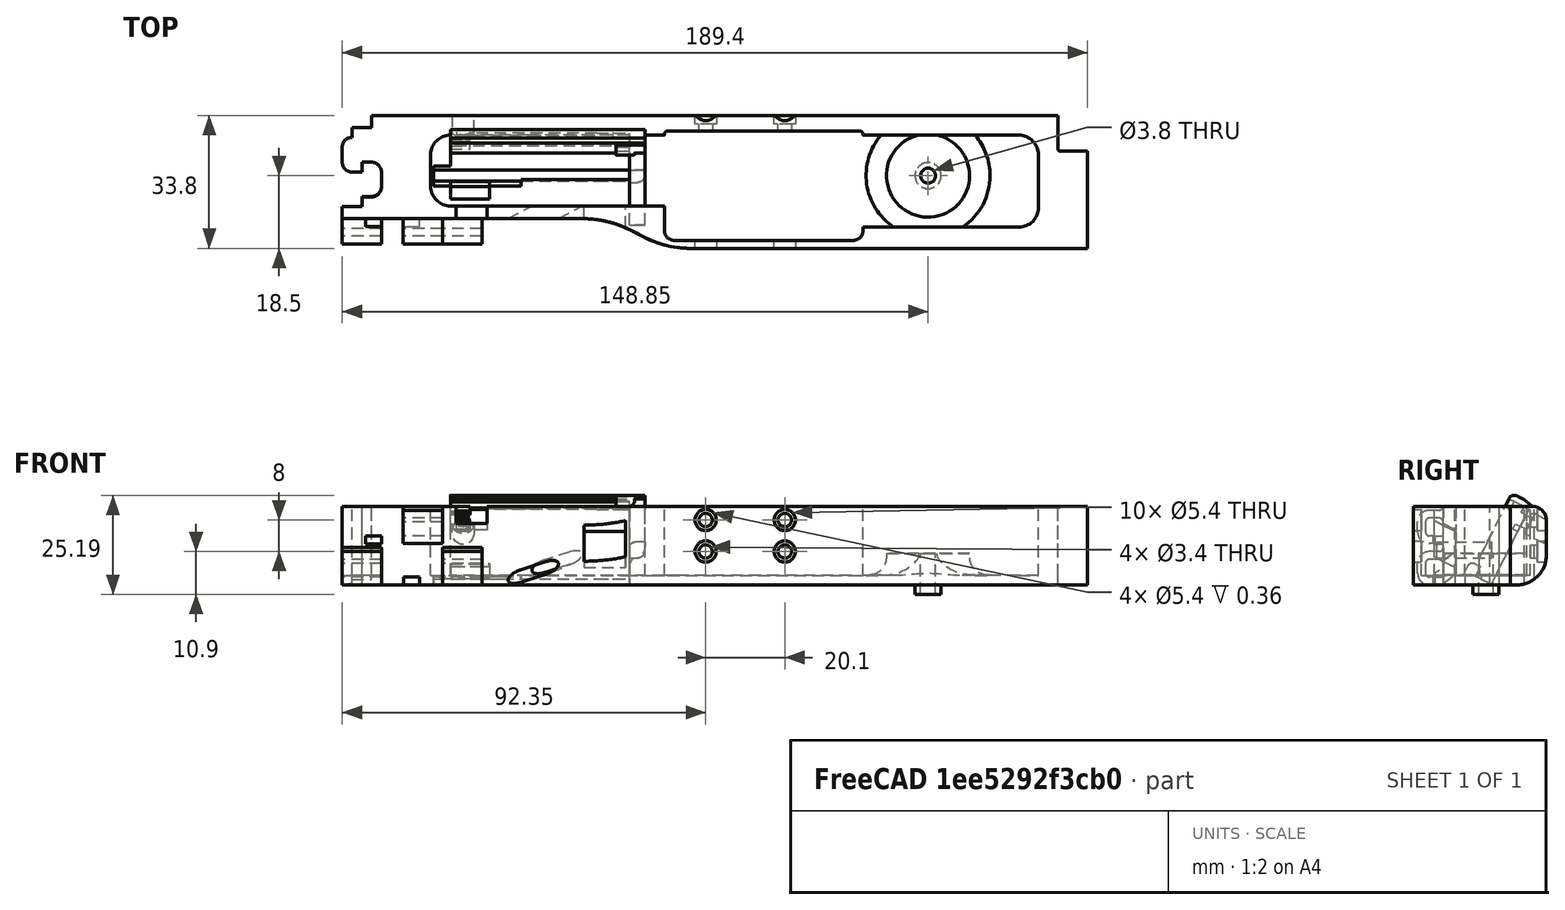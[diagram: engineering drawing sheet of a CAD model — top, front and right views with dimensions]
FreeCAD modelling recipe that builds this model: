
FCSTD DOCUMENT  (FreeCAD 0.19R0.19.2)
Label: rightSideV1_1
License: All rights reserved
LicenseURL: http://en.wikipedia.org/wiki/All_rights_reserved
objects: Sketcher::SketchObject×45, Part::Extrusion×35, Part::MultiFuse×22, Part::Box×19, Part::Cut×16, Part::Fillet×14, App::MeasureDistance×10, Part::Cylinder×4, Part::Revolution×1, Mesh::Feature×1
note: 156 computed .brp shape members not serialized (recipe doc carries the construction recipe); baked Part::Feature solids carry a one-line shape summary decoded from their .brp

FEATURE [Sketcher::SketchObject] Sketch
  FullyConstrained = true
  sketch-geometry (36):
    g0: LineSegment StartX=0 StartY=0 StartZ=0 EndX=154.4 EndY=0 EndZ=0
    g1: LineSegment StartX=154.4 StartY=0 StartZ=0 EndX=154.4 EndY=-7.6 EndZ=0
    g2: LineSegment StartX=32.5209 StartY=-26.2 StartZ=0 EndX=-7.5 EndY=-26.2 EndZ=0
    g3-g7: Circle x5 (B-spline internal-alignment scaffolding for g8; pole/knot coordinates omitted)
    g8: BSplineCurve PolesCount=5 KnotsCount=3 Degree=3 IsPeriodic=0
    g9: GeomPoint X=61.85 Y=-33.8 Z=0
    g10: GeomPoint X=47.185 Y=-29.9 Z=0
    g11: GeomPoint X=32.5209 Y=-26.2 Z=0
    g12: Circle CenterX=121.35 CenterY=-14.3 CenterZ=0 NormalX=0 NormalY=0 NormalZ=1 AngleXU=0 Radius=3.25
    g13: LineSegment StartX=-7.5 StartY=-26.2 StartZ=0 EndX=-27.5 EndY=-26.2 EndZ=0
    g14: LineSegment StartX=-20 StartY=0 StartZ=0 EndX=0 EndY=0 EndZ=0
    g15: LineSegment StartX=-25 StartY=-3.1 StartZ=0 EndX=-20 EndY=-3.1 EndZ=0
    g16: LineSegment StartX=-25 StartY=-3.1 StartZ=0 EndX=-25 EndY=-5.6 EndZ=0
    g17: LineSegment StartX=-27.5 StartY=-8.1 StartZ=0 EndX=-27.5 EndY=-11.85 EndZ=0
    g18: ArcOfCircle CenterX=-25 CenterY=-8.1 CenterZ=0 NormalX=0 NormalY=0 NormalZ=1 AngleXU=0 Radius=2.5 StartAngle=1.5708 EndAngle=3.14159
    g19: LineSegment StartX=-25 StartY=-14.35 StartZ=0 EndX=-22.5 EndY=-14.35 EndZ=0
    g20: ArcOfCircle CenterX=-25 CenterY=-11.85 CenterZ=0 NormalX=0 NormalY=0 NormalZ=1 AngleXU=0 Radius=2.5 StartAngle=3.14159 EndAngle=4.71239
    g21: LineSegment StartX=-22.5 StartY=-14.35 StartZ=0 EndX=-22.5 EndY=-11.85 EndZ=0
    g22: LineSegment StartX=-22.5 StartY=-11.85 StartZ=0 EndX=-20 EndY=-11.85 EndZ=0
    g23: ArcOfCircle CenterX=-20 CenterY=-14.35 CenterZ=0 NormalX=0 NormalY=0 NormalZ=1 AngleXU=0 Radius=2.5 StartAngle=8e-16 EndAngle=1.5708
    g24: LineSegment StartX=-17.5 StartY=-14.35 StartZ=0 EndX=-17.5 EndY=-18.1 EndZ=0
    g25: ArcOfCircle CenterX=-20 CenterY=-18.1 CenterZ=0 NormalX=0 NormalY=0 NormalZ=1 AngleXU=0 Radius=2.5 StartAngle=4.71239 EndAngle=6.28319
    g26: LineSegment StartX=-22.5 StartY=-20.6 StartZ=0 EndX=-20 EndY=-20.6 EndZ=0
    g27: LineSegment StartX=-22.5 StartY=-20.6 StartZ=0 EndX=-22.5 EndY=-23.1 EndZ=0
    g28: LineSegment StartX=-27.5 StartY=-23.1 StartZ=0 EndX=-22.5 EndY=-23.1 EndZ=0
    g29: LineSegment StartX=-20 StartY=-3.1 StartZ=0 EndX=-20 EndY=0 EndZ=0
    g30: LineSegment StartX=-27.5 StartY=-23.1 StartZ=0 EndX=-27.5 EndY=-26.2 EndZ=0
    g31: LineSegment StartX=154.4 StartY=-7.6 StartZ=0 EndX=154.4 EndY=-8.6 EndZ=0
    g32: ArcOfCircle CenterX=154.9 CenterY=-8.6 CenterZ=0 NormalX=0 NormalY=0 NormalZ=1 AngleXU=0 Radius=0.5 StartAngle=3.14159 EndAngle=4.71239
    g33: LineSegment StartX=154.9 StartY=-9.1 StartZ=0 EndX=161.9 EndY=-9.1 EndZ=0
    g34: LineSegment StartX=161.9 StartY=-9.1 StartZ=0 EndX=161.9 EndY=-33.8 EndZ=0
    g35: LineSegment StartX=161.9 StartY=-33.8 StartZ=0 EndX=61.85 EndY=-33.8 EndZ=0
  constraints (72):
    c: PointOnObject(g0,g-2)
    c: Horizontal(g0)
    c: Distance(g0) = 154.4
    c: DistanceY(g-1,g0) = 0
    c: Vertical(g1)
    c: Distance(g1) = 7.6
    c: Coincident(g1,g0)
    c: Horizontal(g2)
    c: Block(g2)
    c: Weight(g3) = 1
    c: Coincident(g8,g2)
    c: InternalAlignment(g3-g7 -> g8) x5
    c: InternalAlignment(g9,g8)
    c: InternalAlignment(g10,g8)
    c: InternalAlignment(g11,g8)
    c: Block(g12)
    c: Coincident(g13,g2)
    c: Horizontal(g13)
    c: Distance(g13) = 20
    c: Horizontal(g14)
    c: Distance(g14) = 20
    c: Coincident(g14,g0)
    c: Horizontal(g15)
    c: Vertical(g16)
    c: Coincident(g16,g15)
    c: Vertical(g17)
    c: Coincident(g18,g16)
    c: Block(g18)
    c: Coincident(g17,g18)
    c: Horizontal(g19)
    c: Coincident(g20,g17)
    c: Block(g20)
    c: Block(g19)
    c: Vertical(g21)
    c: Coincident(g21,g19)
    c: Horizontal(g22)
    c: Coincident(g22,g21)
    c: Coincident(g23,g22)
    c: Vertical(g24)
    c: Block(g23)
    c: Coincident(g24,g23)
    c: Coincident(g25,g24)
    c: Block(g25)
    c: Horizontal(g26)
    c: Coincident(g26,g25)
    c: Vertical(g27)
    c: Coincident(g27,g26)
    c: Horizontal(g28)
    c: Coincident(g28,g27)
    c: Block(g15)
    c: Block(g28)
    c: Coincident(g29,g15)
    c: Coincident(g29,g14)
    c: Vertical(g29)
    c: Coincident(g30,g28)
    c: Coincident(g30,g13)
    c: Vertical(g30)
    c: Vertical(g31)
    c: Distance(g31) = 1
    c: Coincident(g31,g1)
    c: Coincident(g32,g31)
    c: Block(g32)
    c: Coincident(g33,g32)
    c: Horizontal(g33)
    c: Coincident(g34,g33)
    c: Vertical(g34)
    c: Block(g34)
    c: Coincident(g35,g34)
    c: Horizontal(g35)
    c: Block(g35)
    c: Coincident(g8,g35)
    c: Block(g8)
FEATURE [Part::Extrusion] Extrude  label="mainBodyBaseExtrude"
  Base = -> Sketch
  Dir = (0,0,1)
  DirMode = 2
  FaceMakerClass = Part::FaceMakerBullseye
  LengthFwd = 2.4
  LengthRev = 0
  Solid = true
  Symmetric = false
FEATURE [Sketcher::SketchObject] Sketch001
  FullyConstrained = true
  sketch-geometry (75):
    g0: ArcOfCircle CenterX=144.4 CenterY=-10 CenterZ=0 NormalX=0 NormalY=0 NormalZ=1 AngleXU=0 Radius=5 StartAngle=4.345e-13 EndAngle=1.5708
    g1: LineSegment StartX=32.5209 StartY=-26.2 StartZ=0 EndX=-7.49911 EndY=-26.2 EndZ=0
    g2: LineSegment StartX=0 StartY=0 StartZ=0 EndX=154.4 EndY=0 EndZ=0
    g3-g7: Circle x5 (B-spline internal-alignment scaffolding for g8; pole/knot coordinates omitted)
    g8: BSplineCurve PolesCount=5 KnotsCount=3 Degree=3 IsPeriodic=0
    g9: GeomPoint X=61.85 Y=-33.8 Z=0
    g10: GeomPoint X=47.1857 Y=-29.9 Z=0
    g11: GeomPoint X=32.5209 Y=-26.2 Z=0
    g12: LineSegment StartX=154.4 StartY=0 StartZ=0 EndX=154.4 EndY=-7.6 EndZ=0
    g13: LineSegment StartX=20 StartY=-5 StartZ=0 EndX=54.35 EndY=-5 EndZ=0
    g14: LineSegment StartX=104.85 StartY=-5 StartZ=0 EndX=144.4 EndY=-5 EndZ=0
    g15: LineSegment StartX=54.35 StartY=-23 StartZ=0 EndX=20 EndY=-23 EndZ=0
    g16: LineSegment StartX=-27.4991 StartY=-26.2 StartZ=0 EndX=-7.49911 EndY=-26.2 EndZ=0
    g17: LineSegment StartX=-20 StartY=0 StartZ=0 EndX=0 EndY=0 EndZ=0
    g18: LineSegment StartX=-27.4991 StartY=-23.2 StartZ=0 EndX=-22.5 EndY=-23.2 EndZ=0
    g19: LineSegment StartX=-22.5 StartY=-20.7 StartZ=0 EndX=-22.5 EndY=-23.2 EndZ=0
    g20: LineSegment StartX=-22.5 StartY=-20.7 StartZ=0 EndX=-20 EndY=-20.7 EndZ=0
    g21: ArcOfCircle CenterX=-20 CenterY=-18.2 CenterZ=0 NormalX=0 NormalY=0 NormalZ=1 AngleXU=0 Radius=2.5 StartAngle=4.71239 EndAngle=6.28319
    g22: LineSegment StartX=-17.5 StartY=-14.4 StartZ=0 EndX=-17.5 EndY=-18.2 EndZ=0
    g23: ArcOfCircle CenterX=-20 CenterY=-14.4 CenterZ=0 NormalX=0 NormalY=0 NormalZ=1 AngleXU=0 Radius=2.5 StartAngle=9e-16 EndAngle=1.5708
    g24: LineSegment StartX=-22.5 StartY=-11.9 StartZ=0 EndX=-20 EndY=-11.9 EndZ=0
    g25: LineSegment StartX=-22.5 StartY=-14.4 StartZ=0 EndX=-22.5 EndY=-11.9 EndZ=0
    g26: LineSegment StartX=-25 StartY=-14.4 StartZ=0 EndX=-22.5 EndY=-14.4 EndZ=0
    g27: ArcOfCircle CenterX=-25 CenterY=-11.9 CenterZ=0 NormalX=0 NormalY=0 NormalZ=1 AngleXU=0 Radius=2.5 StartAngle=3.14159 EndAngle=4.71239
    g28: LineSegment StartX=-27.5 StartY=-8.1 StartZ=0 EndX=-27.5 EndY=-11.9 EndZ=0
    g29: ArcOfCircle CenterX=-25 CenterY=-8.1 CenterZ=0 NormalX=0 NormalY=0 NormalZ=1 AngleXU=0 Radius=2.5 StartAngle=1.5708 EndAngle=3.14159
    g30: LineSegment StartX=-25 StartY=-3.1 StartZ=0 EndX=-25 EndY=-5.6 EndZ=0
    g31: LineSegment StartX=-20 StartY=-3.1 StartZ=0 EndX=-25 EndY=-3.1 EndZ=0
    g32: LineSegment StartX=-20 StartY=0 StartZ=0 EndX=-20 EndY=-3.1 EndZ=0
    g33: LineSegment StartX=-27.4991 StartY=-26.2 StartZ=0 EndX=-27.4991 EndY=-23.2 EndZ=0
    g34: LineSegment StartX=4.09e-14 StartY=-5 StartZ=0 EndX=20 EndY=-5 EndZ=0
    g35: ArcOfCircle CenterX=7.1e-15 CenterY=-18 CenterZ=0 NormalX=0 NormalY=0 NormalZ=1 AngleXU=0 Radius=5 StartAngle=3.14159 EndAngle=4.71239
    g36: ArcOfCircle CenterX=4.26e-14 CenterY=-10 CenterZ=0 NormalX=0 NormalY=0 NormalZ=1 AngleXU=0 Radius=5 StartAngle=1.5708 EndAngle=3.14159
    g37: LineSegment StartX=-5 StartY=-18 StartZ=0 EndX=-5 EndY=-10 EndZ=0
    g38: LineSegment StartX=6.2e-15 StartY=-23 StartZ=0 EndX=20 EndY=-23 EndZ=0
    g39: LineSegment StartX=154.4 StartY=-7.6 StartZ=0 EndX=154.4 EndY=-8.6 EndZ=0
    g40: LineSegment StartX=154.9 StartY=-9.1 StartZ=0 EndX=161.9 EndY=-9.1 EndZ=0
    g41: ArcOfCircle CenterX=154.9 CenterY=-8.6 CenterZ=0 NormalX=0 NormalY=0 NormalZ=1 AngleXU=0 Radius=0.5 StartAngle=3.14159 EndAngle=4.71299
    g42: LineSegment StartX=104.85 StartY=-28.3916 StartZ=0 EndX=144.408 EndY=-28.3916 EndZ=0
    g43: LineSegment StartX=149.4 StartY=-10 StartZ=0 EndX=149.4 EndY=-23.4 EndZ=0
    g44: ArcOfCircle CenterX=144.408 CenterY=-23.4 CenterZ=0 NormalX=0 NormalY=0 NormalZ=1 AngleXU=0 Radius=4.99164 StartAngle=4.71239 EndAngle=6.28319
    g45: LineSegment StartX=104.85 StartY=-28.3916 StartZ=0 EndX=104.85 EndY=-28.7833 EndZ=0
    g46: LineSegment StartX=54.35 StartY=-28.7916 StartZ=0 EndX=54.35 EndY=-23 EndZ=0
    g47: LineSegment StartX=161.9 StartY=-33.8 StartZ=0 EndX=161.9 EndY=-9.1 EndZ=0
    g48: LineSegment StartX=61.85 StartY=-33.8 StartZ=0 EndX=161.9 EndY=-33.8 EndZ=0
    g49: Circle CenterX=54.35 CenterY=-28.7916 CenterZ=0 NormalX=0 NormalY=0 NormalZ=1 AngleXU=0 Radius=1
    g50: Circle CenterX=54.35 CenterY=-31.7916 CenterZ=0 NormalX=0 NormalY=0 NormalZ=1 AngleXU=0 Radius=1
    g51: Circle CenterX=57.35 CenterY=-31.7916 CenterZ=0 NormalX=0 NormalY=0 NormalZ=1 AngleXU=0 Radius=1
    g52: BSplineCurve PolesCount=3 KnotsCount=2 Degree=2 IsPeriodic=0
    g53: GeomPoint X=54.35 Y=-28.7916 Z=0
    g54: GeomPoint X=57.35 Y=-31.7916 Z=0
    g55: Circle CenterX=104.85 CenterY=-28.7833 CenterZ=0 NormalX=0 NormalY=0 NormalZ=1 AngleXU=0 Radius=1
    g56: Circle CenterX=104.85 CenterY=-31.7916 CenterZ=0 NormalX=0 NormalY=0 NormalZ=1 AngleXU=0 Radius=1
    g57: Circle CenterX=101.85 CenterY=-31.7916 CenterZ=0 NormalX=0 NormalY=0 NormalZ=1 AngleXU=0 Radius=1
    g58: BSplineCurve PolesCount=3 KnotsCount=2 Degree=2 IsPeriodic=0
    g59: GeomPoint X=104.85 Y=-28.7833 Z=0
    g60: GeomPoint X=101.85 Y=-31.7916 Z=0
    g61: LineSegment StartX=57.35 StartY=-31.7916 StartZ=0 EndX=101.85 EndY=-31.7916 EndZ=0
    g62: Circle CenterX=54.35 CenterY=-5 CenterZ=0 NormalX=0 NormalY=0 NormalZ=1 AngleXU=0 Radius=1
    g63: Circle CenterX=54.35 CenterY=-4 CenterZ=0 NormalX=0 NormalY=0 NormalZ=1 AngleXU=0 Radius=1
    g64: Circle CenterX=55.15 CenterY=-4 CenterZ=0 NormalX=0 NormalY=0 NormalZ=1 AngleXU=0 Radius=1
    g65: BSplineCurve PolesCount=3 KnotsCount=2 Degree=2 IsPeriodic=0
    g66: GeomPoint X=54.35 Y=-5 Z=0
    g67: GeomPoint X=55.15 Y=-4 Z=0
    g68: Circle CenterX=104.85 CenterY=-5 CenterZ=0 NormalX=0 NormalY=0 NormalZ=1 AngleXU=0 Radius=1
    g69: Circle CenterX=104.85 CenterY=-4 CenterZ=0 NormalX=0 NormalY=0 NormalZ=1 AngleXU=0 Radius=1
    g70: Circle CenterX=104.05 CenterY=-4 CenterZ=0 NormalX=0 NormalY=0 NormalZ=1 AngleXU=0 Radius=1
    g71: BSplineCurve PolesCount=3 KnotsCount=2 Degree=2 IsPeriodic=0
    g72: GeomPoint X=104.85 Y=-5 Z=0
    g73: GeomPoint X=104.05 Y=-4 Z=0
    g74: LineSegment StartX=104.05 StartY=-4 StartZ=0 EndX=55.15 EndY=-4 EndZ=0
  constraints (156):
    c: PointOnObject(g2,g-2)
    c: DistanceY(g-1,g2) = 0
    c: Block(g0)
    c: Horizontal(g1)
    c: Distance(g1) = 40.02
    c: Horizontal(g2)
    c: Block(g2)
    c: Weight(g3) = 1
    c: Equal(g3, g4-g7) x4
    c: Coincident(g8,g1)
    c: InternalAlignment(g3-g7 -> g8) x5
    c: InternalAlignment(g9,g8)
    c: InternalAlignment(g10,g8)
    c: InternalAlignment(g11,g8)
    c: Vertical(g12)
    c: Coincident(g12,g2)
    c: Distance(g12) = 7.6
    c: Block(g12)
    c: Horizontal(g13)
    c: Coincident(g14,g0)
    c: Horizontal(g14)
    c: Horizontal(g15)
    c: Horizontal(g16)
    c: Distance(g16) = 20
    c: Coincident(g1,g16)
    c: Horizontal(g17)
    c: Distance(g17) = 20
    c: Coincident(g17,g2)
    c: Horizontal(g31)
    c: Vertical(g30)
    c: Coincident(g29,g30)
    c: Vertical(g28)
    c: Block(g29)
    c: Coincident(g27,g28)
    c: Block(g27)
    c: Horizontal(g26)
    c: Coincident(g26,g27)
    c: Vertical(g25)
    c: Coincident(g25,g26)
    c: Horizontal(g24)
    c: Coincident(g23,g24)
    c: Block(g23)
    c: Vertical(g22)
    c: Coincident(g21,g22)
    c: Block(g21)
    c: Horizontal(g20)
    c: Coincident(g20,g21)
    c: Vertical(g19)
    c: Coincident(g19,g20)
    c: Horizontal(g18)
    c: Coincident(g18,g19)
    c: Coincident(g32,g17)
    c: Coincident(g32,g31)
    c: Vertical(g32)
    c: Coincident(g33,g16)
    c: Coincident(g33,g18)
    c: Vertical(g33)
    c: Block(g33)
    c: Block(g18)
    c: Block(g22)
    c: Block(g26)
    c: Block(g25)
    c: Block(g24)
    c: Block(g28)
    c: Block(g31)
    c: Block(g30)
    c: Horizontal(g34)
    c: Distance(g34) = 20
    c: Block(g35)
    c: Block(g36)
    c: Coincident(g37,g35)
    c: Coincident(g37,g36)
    c: Vertical(g37)
    c: Coincident(g38,g35)
    c: Coincident(g38,g15)
    c: Horizontal(g38)
    c: Block(g38)
    c: Block(g34)
    c: Block(g13)
    c: Vertical(g39)
    c: Distance(g39) = 1
    c: Coincident(g39,g12)
    c: Horizontal(g40)
    c: Coincident(g41,g39)
    c: Coincident(g41,g40)
    c: Block(g39)
    c: Block(g41)
    c: Horizontal(g42)
    c: Vertical(g43)
    c: Distance(g43) = 13.4
    c: Coincident(g43,g0)
    c: Block(g42)
    c: Block(g43)
    c: Coincident(g44,g43)
    c: Coincident(g44,g42)
    c: Block(g44)
    c: Distance(g15) = 34.35
    c: Coincident(g45,g42)
    c: Vertical(g45)
    c: Coincident(g46,g15)
    c: Vertical(g46)
    c: Coincident(g47,g40)
    c: Vertical(g47)
    c: Block(g47)
    c: Coincident(g48,g47)
    c: Horizontal(g48)
    c: Block(g48)
    c: Coincident(g8,g48)
    c: Block(g8)
    c: Coincident(g52,g46)
    c: Weight(g49) = 1
    c: Equal(g49,g50)
    c: Equal(g49,g51)
    c: InternalAlignment(g49,g52)
    c: InternalAlignment(g50,g52)
    c: InternalAlignment(g51,g52)
    c: InternalAlignment(g53,g52)
    c: InternalAlignment(g54,g52)
    c: Coincident(g58,g45)
    c: Weight(g55) = 1
    c: Equal(g55,g56)
    c: Equal(g55,g57)
    c: InternalAlignment(g55,g58)
    c: InternalAlignment(g56,g58)
    c: InternalAlignment(g57,g58)
    c: InternalAlignment(g59,g58)
    c: InternalAlignment(g60,g58)
    c: Block(g58)
    c: Block(g52)
    c: Coincident(g61,g52)
    c: Coincident(g61,g58)
    c: Horizontal(g61)
    c: Block(g14)
    c: Coincident(g65,g13)
    c: Weight(g62) = 1
    c: Equal(g62,g63)
    c: Equal(g62,g64)
    c: InternalAlignment(g62,g65)
    c: InternalAlignment(g63,g65)
    c: InternalAlignment(g64,g65)
    c: InternalAlignment(g66,g65)
    c: InternalAlignment(g67,g65)
    c: Block(g65)
    c: Coincident(g71,g14)
    c: Weight(g68) = 1
    c: Equal(g68,g69)
    c: Equal(g68,g70)
    c: InternalAlignment(g68,g71)
    c: InternalAlignment(g69,g71)
    c: InternalAlignment(g70,g71)
    c: InternalAlignment(g72,g71)
    c: InternalAlignment(g73,g71)
    c: Block(g71)
    c: Coincident(g74,g71)
    c: Coincident(g74,g65)
    c: Horizontal(g74)
FEATURE [Sketcher::SketchObject] Sketch005
  FullyConstrained = true
  Placement = pos=(0,0,0) rot=(1,0,0;1.5708rad)
  sketch-geometry (4):
    g0: Circle CenterX=84.95 CenterY=16.5 CenterZ=0 NormalX=0 NormalY=0 NormalZ=1 AngleXU=0 Radius=1.7
    g1: Circle CenterX=84.95 CenterY=8.5 CenterZ=0 NormalX=0 NormalY=0 NormalZ=1 AngleXU=0 Radius=1.7
    g2: Circle CenterX=64.85 CenterY=8.5 CenterZ=0 NormalX=0 NormalY=0 NormalZ=1 AngleXU=0 Radius=1.7
    g3: Circle CenterX=64.85 CenterY=16.5 CenterZ=0 NormalX=0 NormalY=0 NormalZ=1 AngleXU=0 Radius=1.7
  constraints (4):
    c: Block(g0)
    c: Block(g1)
    c: Block(g2)
    c: Block(g3)
FEATURE [Part::Extrusion] Extrude004  label="removeFromMainBodyToCreateScrewHolesForSolenoidExtrude004"
  Base = -> Sketch005
  Dir = (0,-1,1.1e-15)
  DirMode = 2
  FaceMakerClass = Part::FaceMakerBullseye
  LengthFwd = 10
  LengthRev = 0
  Solid = true
  Symmetric = false
FEATURE [Sketcher::SketchObject] Sketch004
  FullyConstrained = true
  Placement = pos=(0,0,0) rot=(1,0,0;1.5708rad)
  sketch-geometry (12):
    g0: LineSegment StartX=15.75 StartY=2.5 StartZ=0 EndX=15.75 EndY=0 EndZ=0
    g1: Circle CenterX=15.75 CenterY=2.5 CenterZ=0 NormalX=0 NormalY=0 NormalZ=1 AngleXU=0 Radius=1
    g2: Circle CenterX=10.55 CenterY=2.5 CenterZ=0 NormalX=0 NormalY=0 NormalZ=1 AngleXU=0 Radius=1
    g3: Circle CenterX=10.55 CenterY=8 CenterZ=0 NormalX=0 NormalY=0 NormalZ=1 AngleXU=0 Radius=1
    g4: BSplineCurve PolesCount=3 KnotsCount=2 Degree=2 IsPeriodic=0
    g5: GeomPoint X=15.75 Y=2.5 Z=0
    g6: GeomPoint X=10.55 Y=8 Z=0
    g7: LineSegment StartX=1.9 StartY=8 StartZ=0 EndX=10.55 EndY=8 EndZ=0
    g8: LineSegment StartX=1.9 StartY=-2.4 StartZ=0 EndX=1.9 EndY=8 EndZ=0
    g9: LineSegment StartX=3.30092 StartY=-2.4 StartZ=0 EndX=3.30092 EndY=0 EndZ=0
    g10: LineSegment StartX=15.75 StartY=0 StartZ=0 EndX=3.30092 EndY=0 EndZ=0
    g11: LineSegment StartX=3.30092 StartY=-2.4 StartZ=0 EndX=1.9 EndY=-2.4 EndZ=0
  constraints (26):
    c: Vertical(g0)
    c: Distance(g0) = 2.5
    c: Coincident(g4,g0)
    c: Weight(g1) = 1
    c: Equal(g1,g2)
    c: Equal(g1,g3)
    c: InternalAlignment(g1,g4)
    c: InternalAlignment(g2,g4)
    c: InternalAlignment(g3,g4)
    c: InternalAlignment(g5,g4)
    c: InternalAlignment(g6,g4)
    c: Block(g4)
    c: Coincident(g7,g4)
    c: Horizontal(g7)
    c: Vertical(g8)
    c: Coincident(g8,g7)
    c: Block(g8)
    c: Vertical(g9)
    c: Coincident(g10,g0)
    c: PointOnObject(g10,g-1)
    c: Horizontal(g10)
    c: Coincident(g10,g9)
    c: Block(g9)
    c: Coincident(g11,g9)
    c: Coincident(g11,g8)
    c: Horizontal(g11)
FEATURE [Sketcher::SketchObject] Sketch007
  FullyConstrained = true
  Placement = pos=(0,-14.3,2.37) rot=(-1,0,0;2.03453rad)
  sketch-geometry (6):
    g0: LineSegment StartX=0 StartY=0 StartZ=0 EndX=45.5 EndY=0 EndZ=0
    g1: LineSegment StartX=0 StartY=0 StartZ=0 EndX=0 EndY=-21.2 EndZ=0
    g2: LineSegment StartX=45.5 StartY=0 StartZ=0 EndX=49.5 EndY=0 EndZ=0
    g3: LineSegment StartX=49.5 StartY=0 StartZ=0 EndX=49.5 EndY=-21.2 EndZ=0
    g4: LineSegment StartX=49.5 StartY=-21.2 StartZ=0 EndX=0 EndY=-21.2 EndZ=0
    g5: Circle CenterX=3.25 CenterY=-18.05 CenterZ=0 NormalX=0 NormalY=0 NormalZ=1 AngleXU=0 Radius=1.6
  constraints (15):
    c: Coincident(g0,g-1)
    c: Horizontal(g0)
    c: Distance(g0) = 45.5
    c: Coincident(g1,g0)
    c: Vertical(g1)
    c: Horizontal(g2)
    c: Distance(g2) = 4
    c: Coincident(g2,g0)
    c: Coincident(g3,g2)
    c: Vertical(g3)
    c: Block(g3)
    c: Coincident(g4,g3)
    c: Horizontal(g4)
    c: Coincident(g4,g1)
    c: Block(g5)
FEATURE [Part::Extrusion] Extrude005  label="solenoidDriverHolderExtrude005"
  Base = -> Sketch007
  Dir = (0,0.894389,-0.447291)
  DirMode = 2
  FaceMakerClass = Part::FaceMakerBullseye
  LengthFwd = 10
  LengthRev = 0
  Placement = pos=(0,0,-2) rot=(0,0,1;0rad)
  Solid = true
  Symmetric = false
FEATURE [Sketcher::SketchObject] Sketch008
  FullyConstrained = false
  Placement = pos=(0,-4.3,-2.6) rot=(-1,0,0;2.03453rad)
  sketch-geometry (1):
    g0: Circle CenterX=42.25 CenterY=-3.15 CenterZ=0 NormalX=0 NormalY=0 NormalZ=1 AngleXU=0 Radius=4.5
FEATURE [Sketcher::SketchObject] Sketch009
  FullyConstrained = true
  Placement = pos=(0,-4.3,-2.6) rot=(-1,0,0;2.03453rad)
  sketch-geometry (1):
    g0: Circle CenterX=3.25 CenterY=-18.0217 CenterZ=0 NormalX=0 NormalY=0 NormalZ=1 AngleXU=0 Radius=2.8
  constraints (1):
    c: Block(g0)
FEATURE [Sketcher::SketchObject] Sketch010
  FullyConstrained = true
  Placement = pos=(0,-14.3,2.37) rot=(-1,0,0;2.03453rad)
  sketch-geometry (1):
    g0: Circle CenterX=3.25 CenterY=-18.05 CenterZ=0 NormalX=0 NormalY=0 NormalZ=1 AngleXU=0 Radius=1.6
  constraints (1):
    c: Block(g0)
FEATURE [Part::Extrusion] Extrude008  label="removeFromScrewHole3"
  Base = -> Sketch010
  Dir = (0,0.894389,-0.447291)
  DirMode = 2
  FaceMakerClass = Part::FaceMakerBullseye
  LengthFwd = -25
  LengthRev = 0
  Placement = pos=(0,4,-4) rot=(0,0,1;0rad)
  Solid = true
  Symmetric = false
FEATURE [Sketcher::SketchObject] Sketch011
  FullyConstrained = true
  Placement = pos=(0,-14.3,2.37) rot=(-1,0,0;2.03453rad)
  sketch-geometry (4):
    g0: LineSegment StartX=49.5 StartY=-21.2 StartZ=0 EndX=49.5 EndY=-22.8 EndZ=0
    g1: LineSegment StartX=49.5 StartY=-22.8 StartZ=0 EndX=0.002238 EndY=-22.8 EndZ=0
    g2: LineSegment StartX=0.002238 StartY=-21.2 StartZ=0 EndX=0.002238 EndY=-22.8 EndZ=0
    g3: LineSegment StartX=49.5 StartY=-21.2 StartZ=0 EndX=0.002238 EndY=-21.2 EndZ=0
  constraints (10):
    c: Vertical(g0)
    c: Distance(g0) = 1.6
    c: Coincident(g1,g0)
    c: Horizontal(g1)
    c: Vertical(g2)
    c: Coincident(g2,g1)
    c: Coincident(g3,g0)
    c: Coincident(g3,g2)
    c: Horizontal(g3)
    c: Block(g3)
FEATURE [Part::Extrusion] Extrude009  label="solenoidDriverTopLipFront"
  Base = -> Sketch011
  Dir = (0,0.894389,-0.447291)
  DirMode = 2
  FaceMakerClass = Part::FaceMakerBullseye
  LengthFwd = -2
  LengthRev = 0
  Placement = pos=(0,-2.9,-0.35) rot=(0,0,1;0rad)
  Solid = true
  Symmetric = false
FEATURE [Sketcher::SketchObject] Sketch012
  FullyConstrained = true
  Placement = pos=(0,-14.3,2.37) rot=(-1,0,0;2.03453rad)
  sketch-geometry (4):
    g0: LineSegment StartX=49.5 StartY=-21.2 StartZ=0 EndX=49.5 EndY=-22.8 EndZ=0
    g1: LineSegment StartX=49.5 StartY=-22.8 StartZ=0 EndX=0.002238 EndY=-22.8 EndZ=0
    g2: LineSegment StartX=0.002238 StartY=-21.2 StartZ=0 EndX=0.002238 EndY=-22.8 EndZ=0
    g3: LineSegment StartX=49.5 StartY=-21.2 StartZ=0 EndX=0.002238 EndY=-21.2 EndZ=0
  constraints (10):
    c: Vertical(g0)
    c: Distance(g0) = 1.6
    c: Coincident(g1,g0)
    c: Horizontal(g1)
    c: Vertical(g2)
    c: Coincident(g2,g1)
    c: Coincident(g3,g0)
    c: Coincident(g3,g2)
    c: Horizontal(g3)
    c: Block(g3)
FEATURE [Part::Extrusion] Extrude010  label="solenoidDriverTopLipLowerExtrude010"
  Base = -> Sketch012
  Dir = (0,0.894389,-0.447291)
  DirMode = 2
  FaceMakerClass = Part::FaceMakerBullseye
  LengthFwd = 5.05
  LengthRev = 0
  Solid = true
  Symmetric = false
FEATURE [Sketcher::SketchObject] Sketch015
  FullyConstrained = true
  Placement = pos=(0,-14.3,2.37) rot=(-1,0,0;2.03453rad)
  sketch-geometry (4):
    g0: LineSegment StartX=0 StartY=1.5 StartZ=0 EndX=0 EndY=0 EndZ=0
    g1: LineSegment StartX=0 StartY=1.5 StartZ=0 EndX=5 EndY=1.5 EndZ=0
    g2: LineSegment StartX=5 StartY=1.5 StartZ=0 EndX=5 EndY=0 EndZ=0
    g3: LineSegment StartX=0 StartY=0 StartZ=0 EndX=5 EndY=0 EndZ=0
  constraints (13):
    c: Vertical(g0)
    c: Distance(g0) = 1.5
    c: Horizontal(g1)
    c: Distance(g1) = 5
    c: Coincident(g1,g0)
    c: Vertical(g2)
    c: Distance(g2) = 1.5
    c: Coincident(g2,g1)
    c: Block(g1)
    c: Block(g2)
    c: Block(g0)
    c: Coincident(g3,g0)
    c: Coincident(g3,g2)
FEATURE [Part::Extrusion] Extrude013  label="solenoidDriverBottomLipTopExtrude012"
  Base = -> Sketch015
  Dir = (0,0.894389,-0.447291)
  DirMode = 2
  FaceMakerClass = Part::FaceMakerBullseye
  LengthFwd = -6.5
  LengthRev = 0
  Placement = pos=(0,-14.15,19.65) rot=(1,0,0;1.5708rad)
  Solid = true
  Symmetric = false
FEATURE [Sketcher::SketchObject] Sketch016
  FullyConstrained = true
  Placement = pos=(0,0,0) rot=(1,0,0;1.5708rad)
  sketch-geometry (4):
    g0: Circle CenterX=84.15 CenterY=16.5 CenterZ=0 NormalX=0 NormalY=0 NormalZ=1 AngleXU=0 Radius=2.7
    g1: Circle CenterX=64.05 CenterY=16.5 CenterZ=0 NormalX=0 NormalY=0 NormalZ=1 AngleXU=0 Radius=2.7
    g2: Circle CenterX=64.05 CenterY=8.5 CenterZ=0 NormalX=0 NormalY=0 NormalZ=1 AngleXU=0 Radius=2.7
    g3: Circle CenterX=84.15 CenterY=8.5 CenterZ=0 NormalX=0 NormalY=0 NormalZ=1 AngleXU=0 Radius=2.7
  constraints (4):
    c: Block(g0)
    c: Block(g1)
    c: Block(g3)
    c: Block(g2)
FEATURE [Part::Extrusion] Extrude014  label="removeFromMainBodyToCreateScrewHoleCounterSinks"
  Base = -> Sketch016
  Dir = (0,-1,1.1e-15)
  DirMode = 2
  FaceMakerClass = Part::FaceMakerBullseye
  LengthFwd = 1.9
  LengthRev = 0
  Placement = pos=(0.8,-0.36,0) rot=(0,0,1;0rad)
  Solid = true
  Symmetric = false
FEATURE [Part::Extrusion] Extrude015  label="removeFromScrewHole2Extrude007"
  Base = -> Sketch009
  Dir = (0,0.894389,-0.447291)
  DirMode = 2
  FaceMakerClass = Part::FaceMakerBullseye
  LengthFwd = 10
  LengthRev = 0
  Placement = pos=(0,-8,2) rot=(0,0,1;0rad)
  Solid = true
  Symmetric = false
FEATURE [Sketcher::SketchObject] Sketch017
  FullyConstrained = true
  Placement = pos=(0,-14.3,2.37) rot=(-1,0,0;2.03453rad)
  sketch-geometry (4):
    g0: LineSegment StartX=0 StartY=1.5 StartZ=0 EndX=0 EndY=0 EndZ=0
    g1: LineSegment StartX=0 StartY=1.5 StartZ=0 EndX=5 EndY=1.5 EndZ=0
    g2: LineSegment StartX=5 StartY=1.5 StartZ=0 EndX=5 EndY=0 EndZ=0
    g3: LineSegment StartX=0 StartY=0 StartZ=0 EndX=5 EndY=0 EndZ=0
  constraints (13):
    c: Vertical(g0)
    c: Distance(g0) = 1.5
    c: Horizontal(g1)
    c: Distance(g1) = 5
    c: Coincident(g1,g0)
    c: Vertical(g2)
    c: Distance(g2) = 1.5
    c: Coincident(g2,g1)
    c: Block(g1)
    c: Block(g2)
    c: Block(g0)
    c: Coincident(g3,g0)
    c: Coincident(g3,g2)
FEATURE [Part::Extrusion] Extrude016  label="solenoidDriverBottomLipTopExtrude013"
  Base = -> Sketch017
  Dir = (0,0.894389,-0.447291)
  DirMode = 2
  FaceMakerClass = Part::FaceMakerBullseye
  LengthFwd = -6.5
  LengthRev = 0
  Placement = pos=(0,-15.45,20.3) rot=(1,0,0;1.5708rad)
  Solid = true
  Symmetric = false
FEATURE [Part::Fillet] Fillet005  label="solenoidDriverBottomLipTopFillet005"
  Base = -> Extrude016
  Edges = 1 edges r=1.4: [Edge6]
FEATURE [Sketcher::SketchObject] Sketch018
  FullyConstrained = true
  Placement = pos=(38.5,-14.3,2.37) rot=(-1,0,0;2.03453rad)
  sketch-geometry (4):
    g0: LineSegment StartX=11 StartY=0 StartZ=0 EndX=11 EndY=1.5 EndZ=0
    g1: LineSegment StartX=11 StartY=0 StartZ=0 EndX=3.6 EndY=0 EndZ=0
    g2: LineSegment StartX=3.6 StartY=0 StartZ=0 EndX=3.6 EndY=1.5 EndZ=0
    g3: LineSegment StartX=11 StartY=1.5 StartZ=0 EndX=3.6 EndY=1.5 EndZ=0
  constraints (12):
    c: PointOnObject(g0,g-1)
    c: Vertical(g0)
    c: Distance(g0) = 1.5
    c: Horizontal(g1)
    c: Distance(g1) = 7.4
    c: Coincident(g1,g0)
    c: Block(g0)
    c: Coincident(g2,g1)
    c: Vertical(g2)
    c: Coincident(g3,g0)
    c: Horizontal(g3)
    c: Coincident(g2,g3)
FEATURE [Part::Extrusion] Extrude017
  Base = -> Sketch018
  Dir = (0,0.894389,-0.447291)
  DirMode = 2
  FaceMakerClass = Part::FaceMakerBullseye
  LengthFwd = 4
  LengthRev = 0
  Placement = pos=(0,-8.212,34.025) rot=(1,0,0;1.5708rad)
  Solid = true
  Symmetric = false
FEATURE [Sketcher::SketchObject] Sketch019
  FullyConstrained = true
  Placement = pos=(0,0,0) rot=(1,0,0;1.5708rad)
  sketch-geometry (4):
    g0: Circle CenterX=84.95 CenterY=8.5 CenterZ=0 NormalX=0 NormalY=0 NormalZ=1 AngleXU=0 Radius=2.7
    g1: Circle CenterX=64.85 CenterY=8.5 CenterZ=0 NormalX=0 NormalY=0 NormalZ=1 AngleXU=0 Radius=2.7
    g2: Circle CenterX=64.85 CenterY=16.5 CenterZ=0 NormalX=0 NormalY=0 NormalZ=1 AngleXU=0 Radius=2.7
    g3: Circle CenterX=84.95 CenterY=16.5 CenterZ=0 NormalX=0 NormalY=0 NormalZ=1 AngleXU=0 Radius=2.7
  constraints (4):
    c: Block(g3)
    c: Block(g2)
    c: Block(g0)
    c: Block(g1)
FEATURE [Part::Extrusion] Extrude019  label="removeSolenoidAdjusterHoles"
  Base = -> Sketch019
  Dir = (0,-1,1.1e-15)
  DirMode = 2
  FaceMakerClass = Part::FaceMakerBullseye
  LengthFwd = 6
  LengthRev = 0
  Placement = pos=(0,-30,0) rot=(0,0,1;0rad)
  Solid = true
  Symmetric = false
FEATURE [Sketcher::SketchObject] Sketch020
  FullyConstrained = true
  Placement = pos=(0,-14.3,2.37) rot=(-1,0,0;2.03453rad)
  sketch-geometry (6):
    g0: LineSegment StartX=45.5 StartY=-21.2 StartZ=0 EndX=49.5 EndY=-21.2 EndZ=0
    g1: LineSegment StartX=45.5 StartY=0 StartZ=0 EndX=49.5 EndY=0 EndZ=0
    g2: LineSegment StartX=49.5 StartY=0 StartZ=0 EndX=49.5 EndY=-21.2 EndZ=0
    g3: LineSegment StartX=4 StartY=0 StartZ=0 EndX=4 EndY=-21.2 EndZ=0
    g4: LineSegment StartX=45.5 StartY=-21.2 StartZ=0 EndX=4 EndY=-21.2 EndZ=0
    g5: LineSegment StartX=4 StartY=0 StartZ=0 EndX=45.5 EndY=0 EndZ=0
  constraints (16):
    c: Horizontal(g0)
    c: Distance(g0) = 4
    c: Horizontal(g1)
    c: Distance(g1) = 4
    c: Coincident(g2,g1)
    c: Coincident(g2,g0)
    c: Vertical(g2)
    c: Block(g2)
    c: Vertical(g3)
    c: Coincident(g4,g0)
    c: Horizontal(g4)
    c: Coincident(g4,g3)
    c: Coincident(g5,g1)
    c: Horizontal(g5)
    c: Block(g3)
    c: Block(g5)
FEATURE [Part::Box] Box  label="Cube"
  AttacherType = Attacher::AttachEngine3D
  Height = 10
  Length = 190
  Placement = pos=(-30,0,0) rot=(0,0,1;0rad)
  Width = 10
FEATURE [Part::Fillet] Fillet008
  Base = -> Box
  Edges = 1 edges r=7.5: [Edge11]
FEATURE [Part::Box] Box001  label="Cube001"
  AttacherType = Attacher::AttachEngine3D
  Height = 10
  Length = 190
  Placement = pos=(-35,0,0) rot=(0,0,1;0rad)
  Width = 10
FEATURE [Part::Cut] Cut  label="filletMain"
  Base = -> Box001
  Placement = pos=(0,-10,0) rot=(0,0,1;0rad)
  Tool = -> Fillet008
FEATURE [Part::Box] Box002  label="Cube002"
  AttacherType = Attacher::AttachEngine3D
  Height = 30
  Length = 190
  Placement = pos=(-20,0,0) rot=(0,0,1;0rad)
  Width = 10
FEATURE [Part::Box] Box003  label="Cube003"
  AttacherType = Attacher::AttachEngine3D
  Height = 10
  Length = 190
  Placement = pos=(-90,-50,-10) rot=(0,0,1;0rad)
  Width = 50
FEATURE [Sketcher::SketchObject] Sketch021
  FullyConstrained = true
  Placement = pos=(0,-14.3,2.37) rot=(-1,0,0;2.03453rad)
  sketch-geometry (6):
    g0: LineSegment StartX=41.65 StartY=-3.15 StartZ=0 EndX=38.95 EndY=-3.15 EndZ=0
    g1: LineSegment StartX=36.25 StartY=-3.15 StartZ=0 EndX=38.95 EndY=-3.15 EndZ=0
    g2: LineSegment StartX=41.65 StartY=-3.15 StartZ=0 EndX=41.65 EndY=-7.15 EndZ=0
    g3: LineSegment StartX=38.95 StartY=-7.15 StartZ=0 EndX=41.65 EndY=-7.15 EndZ=0
    g4: LineSegment StartX=38.95 StartY=-7.15 StartZ=0 EndX=36.25 EndY=-7.15 EndZ=0
    g5: LineSegment StartX=36.25 StartY=-3.15 StartZ=0 EndX=36.25 EndY=-7.15 EndZ=0
  constraints (16):
    c: Horizontal(g0)
    c: Distance(g0) = 2.7
    c: Horizontal(g1)
    c: Distance(g1) = 2.7
    c: Coincident(g1,g0)
    c: Block(g0)
    c: Coincident(g2,g0)
    c: Vertical(g2)
    c: Horizontal(g3)
    c: Coincident(g3,g2)
    c: Horizontal(g4)
    c: Coincident(g5,g1)
    c: Vertical(g5)
    c: Coincident(g5,g4)
    c: Block(g3)
    c: Block(g4)
FEATURE [Sketcher::SketchObject] Sketch022
  FullyConstrained = true
  Placement = pos=(0,-14.3,2.37) rot=(-1,0,0;2.03453rad)
  sketch-geometry (6):
    g0: LineSegment StartX=41.65 StartY=-3.15 StartZ=0 EndX=38.95 EndY=-3.15 EndZ=0
    g1: LineSegment StartX=36.25 StartY=-3.15 StartZ=0 EndX=38.95 EndY=-3.15 EndZ=0
    g2: LineSegment StartX=41.65 StartY=-3.15 StartZ=0 EndX=41.65 EndY=-7.15 EndZ=0
    g3: LineSegment StartX=38.95 StartY=-7.15 StartZ=0 EndX=41.65 EndY=-7.15 EndZ=0
    g4: LineSegment StartX=38.95 StartY=-7.15 StartZ=0 EndX=36.25 EndY=-7.15 EndZ=0
    g5: LineSegment StartX=36.25 StartY=-3.15 StartZ=0 EndX=36.25 EndY=-7.15 EndZ=0
  constraints (16):
    c: Horizontal(g0)
    c: Distance(g0) = 2.7
    c: Horizontal(g1)
    c: Distance(g1) = 2.7
    c: Coincident(g1,g0)
    c: Block(g0)
    c: Coincident(g2,g0)
    c: Vertical(g2)
    c: Horizontal(g3)
    c: Coincident(g3,g2)
    c: Horizontal(g4)
    c: Coincident(g5,g1)
    c: Vertical(g5)
    c: Coincident(g5,g4)
    c: Block(g3)
    c: Block(g4)
FEATURE [Sketcher::SketchObject] Sketch024
  FullyConstrained = true
  Placement = pos=(0,-14.3,2.37) rot=(-1,0,0;2.03453rad)
  sketch-geometry (4):
    g0: LineSegment StartX=49.5 StartY=-21.2 StartZ=0 EndX=49.5 EndY=-22.8 EndZ=0
    g1: LineSegment StartX=49.5 StartY=-22.8 StartZ=0 EndX=0.002238 EndY=-22.8 EndZ=0
    g2: LineSegment StartX=0.002238 StartY=-21.2 StartZ=0 EndX=0.002238 EndY=-22.8 EndZ=0
    g3: LineSegment StartX=49.5 StartY=-21.2 StartZ=0 EndX=0.002238 EndY=-21.2 EndZ=0
  constraints (10):
    c: Vertical(g0)
    c: Distance(g0) = 1.6
    c: Coincident(g1,g0)
    c: Horizontal(g1)
    c: Vertical(g2)
    c: Coincident(g2,g1)
    c: Coincident(g3,g0)
    c: Coincident(g3,g2)
    c: Horizontal(g3)
    c: Block(g3)
FEATURE [Sketcher::SketchObject] Sketch025
  FullyConstrained = true
  Placement = pos=(0,-14.3,2.37) rot=(-1,0,0;2.03453rad)
  sketch-geometry (4):
    g0: LineSegment StartX=0 StartY=1.5 StartZ=0 EndX=0 EndY=0 EndZ=0
    g1: LineSegment StartX=0 StartY=1.5 StartZ=0 EndX=5 EndY=1.5 EndZ=0
    g2: LineSegment StartX=5 StartY=1.5 StartZ=0 EndX=5 EndY=0 EndZ=0
    g3: LineSegment StartX=0 StartY=0 StartZ=0 EndX=5 EndY=0 EndZ=0
  constraints (13):
    c: Vertical(g0)
    c: Distance(g0) = 1.5
    c: Horizontal(g1)
    c: Distance(g1) = 5
    c: Coincident(g1,g0)
    c: Vertical(g2)
    c: Distance(g2) = 1.5
    c: Coincident(g2,g1)
    c: Block(g1)
    c: Block(g2)
    c: Block(g0)
    c: Coincident(g3,g0)
    c: Coincident(g3,g2)
FEATURE [Part::Extrusion] Extrude022  label="solenoidDriverBottomLipTopExtrude014"
  Base = -> Sketch025
  Dir = (0,0.894389,-0.447291)
  DirMode = 2
  FaceMakerClass = Part::FaceMakerBullseye
  LengthFwd = -6.5
  LengthRev = 0
  Placement = pos=(0,-15.45,20.3) rot=(1,0,0;1.5708rad)
  Solid = true
  Symmetric = false
FEATURE [Part::Fillet] Fillet013  label="solenoidDriverBottomLipTopFillet006"
  Base = -> Extrude022
  Edges = 1 edges r=1.4: [Edge6]
  Placement = pos=(5,0,0) rot=(0,0,1;0rad)
FEATURE [Sketcher::SketchObject] Sketch026
  FullyConstrained = true
  Placement = pos=(0,-14.3,2.37) rot=(-1,0,0;2.03453rad)
  sketch-geometry (4):
    g0: LineSegment StartX=0 StartY=1.5 StartZ=0 EndX=0 EndY=0 EndZ=0
    g1: LineSegment StartX=0 StartY=1.5 StartZ=0 EndX=5 EndY=1.5 EndZ=0
    g2: LineSegment StartX=5 StartY=1.5 StartZ=0 EndX=5 EndY=0 EndZ=0
    g3: LineSegment StartX=0 StartY=0 StartZ=0 EndX=5 EndY=0 EndZ=0
  constraints (13):
    c: Vertical(g0)
    c: Distance(g0) = 1.5
    c: Horizontal(g1)
    c: Distance(g1) = 5
    c: Coincident(g1,g0)
    c: Vertical(g2)
    c: Distance(g2) = 1.5
    c: Coincident(g2,g1)
    c: Block(g1)
    c: Block(g2)
    c: Block(g0)
    c: Coincident(g3,g0)
    c: Coincident(g3,g2)
FEATURE [Part::Extrusion] Extrude023  label="solenoidDriverBottomLipTopExtrude015"
  Base = -> Sketch026
  Dir = (0,0.894389,-0.447291)
  DirMode = 2
  FaceMakerClass = Part::FaceMakerBullseye
  LengthFwd = -6.5
  LengthRev = 0
  Placement = pos=(5,-14.15,19.65) rot=(1,0,0;1.5708rad)
  Solid = true
  Symmetric = false
FEATURE [Sketcher::SketchObject] Sketch027
  FullyConstrained = true
  Placement = pos=(0,-14.3,2.37) rot=(-1,0,0;2.03453rad)
  sketch-geometry (5):
    g0: LineSegment StartX=45.5 StartY=-21.2 StartZ=0 EndX=49.5 EndY=-21.2 EndZ=0
    g1: LineSegment StartX=49.5 StartY=0 StartZ=0 EndX=49.5 EndY=-21.2 EndZ=0
    g2: LineSegment StartX=49.5 StartY=0 StartZ=0 EndX=49.5 EndY=1.6 EndZ=0
    g3: LineSegment StartX=45.5 StartY=-21.2 StartZ=0 EndX=45.5 EndY=1.6 EndZ=0
    g4: LineSegment StartX=49.5 StartY=1.6 StartZ=0 EndX=45.5 EndY=1.6 EndZ=0
  constraints (14):
    c: Horizontal(g0)
    c: Distance(g0) = 4
    c: Coincident(g1,g0)
    c: Vertical(g1)
    c: Block(g1)
    c: Vertical(g2)
    c: Distance(g2) = 1.6
    c: Block(g2)
    c: Coincident(g3,g0)
    c: Vertical(g3)
    c: Coincident(g4,g2)
    c: Horizontal(g4)
    c: Block(g0)
    c: Coincident(g3,g4)
FEATURE [Part::Extrusion] Extrude024
  Base = -> Sketch027
  Dir = (0,0.894389,-0.447291)
  DirMode = 2
  FaceMakerClass = Part::FaceMakerBullseye
  LengthFwd = 6.34
  LengthRev = 0
  Placement = pos=(0,-5.59,1) rot=(0,0,1;0rad)
  Solid = true
  Symmetric = false
FEATURE [Part::Fillet] Fillet014  label="solenoidDriverSideBarFillet014"
  Base = -> Extrude024
  Edges = 1 edges r=1.4: [Edge14]
  Placement = pos=(0,0.9,-0.45) rot=(0,0,1;0rad)
FEATURE [Part::Revolution] Revolve  label="mainScrewStandRevolve"
  Angle = 360
  Axis = (0,0,1)
  Base = (0,0,0)
  FaceMakerClass = Part::FaceMakerBullseye
  Placement = pos=(121.35,-15.3,0) rot=(0,0,1;0rad)
  Solid = true
  Source = -> Sketch004
  Symmetric = false
FEATURE [Part::Extrusion] Extrude021  label="solenoidDriverTopLipLowerExtrude011"
  Base = -> Sketch024
  Dir = (0,0.894389,-0.447291)
  DirMode = 2
  FaceMakerClass = Part::FaceMakerBullseye
  LengthFwd = 5.05
  LengthRev = 0
  Solid = true
  Symmetric = false
FEATURE [Part::Fillet] Fillet012  label="solenoidDriverTopLipLowerFillet004"
  Base = -> Extrude021
  Edges = 1 edges r=1.2: [Edge7]
  Placement = pos=(0,-0.9,-1.35) rot=(0,0,1;0rad)
FEATURE [Part::Fillet] Fillet003  label="solenoidDriverTopLipLowerFillet003"
  Base = -> Extrude010
  Edges = 1 edges r=1.2: [Edge7]
  Placement = pos=(0,-3,-0.3) rot=(0,0,1;0rad)
FEATURE [Part::Extrusion] Extrude025  label="mainBodyUpperExtrude025"
  Base = -> Sketch001
  Dir = (0,0,1)
  DirMode = 2
  FaceMakerClass = Part::FaceMakerBullseye
  LengthFwd = 20
  LengthRev = 0
  Solid = true
  Symmetric = false
FEATURE [Part::MultiFuse] Fusion  label="solenoidDriverBottomLipFusion"
  Placement = pos=(0,-1.6,0) rot=(0,0,1;0rad)
  Shapes = -> [Fillet005,Fillet013,Extrude023,Extrude013]
FEATURE [Sketcher::SketchObject] Sketch028
  FullyConstrained = true
  Placement = pos=(0,-14.3,2.37) rot=(-1,0,0;2.03453rad)
  sketch-geometry (4):
    g0: LineSegment StartX=0 StartY=1.5 StartZ=0 EndX=0 EndY=0 EndZ=0
    g1: LineSegment StartX=0 StartY=1.5 StartZ=0 EndX=5 EndY=1.5 EndZ=0
    g2: LineSegment StartX=5 StartY=1.5 StartZ=0 EndX=5 EndY=0 EndZ=0
    g3: LineSegment StartX=0 StartY=0 StartZ=0 EndX=5 EndY=0 EndZ=0
  constraints (13):
    c: Vertical(g0)
    c: Distance(g0) = 1.5
    c: Horizontal(g1)
    c: Distance(g1) = 5
    c: Coincident(g1,g0)
    c: Vertical(g2)
    c: Distance(g2) = 1.5
    c: Coincident(g2,g1)
    c: Block(g1)
    c: Block(g2)
    c: Block(g0)
    c: Coincident(g3,g0)
    c: Coincident(g3,g2)
FEATURE [Part::Extrusion] Extrude026  label="solenoidDriverBottomLipTopExtrude016"
  Base = -> Sketch028
  Dir = (0,0.894389,-0.447291)
  DirMode = 2
  FaceMakerClass = Part::FaceMakerBullseye
  LengthFwd = -6.5
  LengthRev = 0
  Placement = pos=(5,-14.15,19.65) rot=(1,0,0;1.5708rad)
  Solid = true
  Symmetric = false
FEATURE [Sketcher::SketchObject] Sketch029
  FullyConstrained = true
  Placement = pos=(0,-14.3,2.37) rot=(-1,0,0;2.03453rad)
  sketch-geometry (4):
    g0: LineSegment StartX=0 StartY=1.5 StartZ=0 EndX=0 EndY=0 EndZ=0
    g1: LineSegment StartX=0 StartY=1.5 StartZ=0 EndX=5 EndY=1.5 EndZ=0
    g2: LineSegment StartX=5 StartY=1.5 StartZ=0 EndX=5 EndY=0 EndZ=0
    g3: LineSegment StartX=0 StartY=0 StartZ=0 EndX=5 EndY=0 EndZ=0
  constraints (13):
    c: Vertical(g0)
    c: Distance(g0) = 1.5
    c: Horizontal(g1)
    c: Distance(g1) = 5
    c: Coincident(g1,g0)
    c: Vertical(g2)
    c: Distance(g2) = 1.5
    c: Coincident(g2,g1)
    c: Block(g1)
    c: Block(g2)
    c: Block(g0)
    c: Coincident(g3,g0)
    c: Coincident(g3,g2)
FEATURE [Part::Extrusion] Extrude027  label="solenoidDriverBottomLipTopExtrude017"
  Base = -> Sketch029
  Dir = (0,0.894389,-0.447291)
  DirMode = 2
  FaceMakerClass = Part::FaceMakerBullseye
  LengthFwd = -6.5
  LengthRev = 0
  Placement = pos=(0,-14.15,19.65) rot=(1,0,0;1.5708rad)
  Solid = true
  Symmetric = false
FEATURE [Sketcher::SketchObject] Sketch030
  FullyConstrained = true
  Placement = pos=(0,-14.3,2.37) rot=(-1,0,0;2.03453rad)
  sketch-geometry (4):
    g0: LineSegment StartX=0 StartY=1.5 StartZ=0 EndX=0 EndY=0 EndZ=0
    g1: LineSegment StartX=0 StartY=1.5 StartZ=0 EndX=5 EndY=1.5 EndZ=0
    g2: LineSegment StartX=5 StartY=1.5 StartZ=0 EndX=5 EndY=0 EndZ=0
    g3: LineSegment StartX=0 StartY=0 StartZ=0 EndX=5 EndY=0 EndZ=0
  constraints (13):
    c: Vertical(g0)
    c: Distance(g0) = 1.5
    c: Horizontal(g1)
    c: Distance(g1) = 5
    c: Coincident(g1,g0)
    c: Vertical(g2)
    c: Distance(g2) = 1.5
    c: Coincident(g2,g1)
    c: Block(g1)
    c: Block(g2)
    c: Block(g0)
    c: Coincident(g3,g0)
    c: Coincident(g3,g2)
FEATURE [Sketcher::SketchObject] Sketch031
  FullyConstrained = true
  Placement = pos=(0,-14.3,2.37) rot=(-1,0,0;2.03453rad)
  sketch-geometry (6):
    g0: LineSegment StartX=45.5 StartY=-21.2 StartZ=0 EndX=49.5 EndY=-21.2 EndZ=0
    g1: LineSegment StartX=45.5 StartY=0 StartZ=0 EndX=49.5 EndY=0 EndZ=0
    g2: LineSegment StartX=49.5 StartY=0 StartZ=0 EndX=49.5 EndY=-21.2 EndZ=0
    g3: LineSegment StartX=4 StartY=0 StartZ=0 EndX=4 EndY=-21.2 EndZ=0
    g4: LineSegment StartX=45.5 StartY=-21.2 StartZ=0 EndX=4 EndY=-21.2 EndZ=0
    g5: LineSegment StartX=4 StartY=0 StartZ=0 EndX=45.5 EndY=0 EndZ=0
  constraints (16):
    c: Horizontal(g0)
    c: Distance(g0) = 4
    c: Horizontal(g1)
    c: Distance(g1) = 4
    c: Coincident(g2,g1)
    c: Coincident(g2,g0)
    c: Vertical(g2)
    c: Block(g2)
    c: Vertical(g3)
    c: Coincident(g4,g0)
    c: Horizontal(g4)
    c: Coincident(g4,g3)
    c: Coincident(g5,g1)
    c: Horizontal(g5)
    c: Block(g3)
    c: Block(g5)
FEATURE [Part::Extrusion] Extrude028  label="removeFromSolenoidDriverMainExtrude021"
  Base = -> Sketch031
  Dir = (0,0.894389,-0.447291)
  DirMode = 2
  FaceMakerClass = Part::FaceMakerBullseye
  LengthFwd = 3.1
  LengthRev = 0
  Placement = pos=(-4,-2.42,-0.8) rot=(0,0,1;0rad)
  Solid = true
  Symmetric = false
FEATURE [Part::Extrusion] Extrude029  label="solenoidDriverBottomLipTopExtrude018"
  Base = -> Sketch030
  Dir = (0,0.894389,-0.447291)
  DirMode = 2
  FaceMakerClass = Part::FaceMakerBullseye
  LengthFwd = -6.5
  LengthRev = 0
  Placement = pos=(5,-14.15,19.65) rot=(1,0,0;1.5708rad)
  Solid = true
  Symmetric = false
FEATURE [Sketcher::SketchObject] Sketch032
  FullyConstrained = true
  Placement = pos=(0,-14.3,2.37) rot=(-1,0,0;2.03453rad)
  sketch-geometry (4):
    g0: LineSegment StartX=0 StartY=1.5 StartZ=0 EndX=0 EndY=0 EndZ=0
    g1: LineSegment StartX=0 StartY=1.5 StartZ=0 EndX=5 EndY=1.5 EndZ=0
    g2: LineSegment StartX=5 StartY=1.5 StartZ=0 EndX=5 EndY=0 EndZ=0
    g3: LineSegment StartX=0 StartY=0 StartZ=0 EndX=5 EndY=0 EndZ=0
  constraints (13):
    c: Vertical(g0)
    c: Distance(g0) = 1.5
    c: Horizontal(g1)
    c: Distance(g1) = 5
    c: Coincident(g1,g0)
    c: Vertical(g2)
    c: Distance(g2) = 1.5
    c: Coincident(g2,g1)
    c: Block(g1)
    c: Block(g2)
    c: Block(g0)
    c: Coincident(g3,g0)
    c: Coincident(g3,g2)
FEATURE [Part::Extrusion] Extrude030  label="solenoidDriverBottomLipTopExtrude019"
  Base = -> Sketch032
  Dir = (0,0.894389,-0.447291)
  DirMode = 2
  FaceMakerClass = Part::FaceMakerBullseye
  LengthFwd = -6.5
  LengthRev = 0
  Placement = pos=(0,-14.15,19.65) rot=(1,0,0;1.5708rad)
  Solid = true
  Symmetric = false
FEATURE [Part::MultiFuse] Fusion004
  Placement = pos=(0,1.4,2.65) rot=(0,0,1;0rad)
  Shapes = -> [Extrude029,Extrude030]
FEATURE [Part::MultiFuse] Fusion003
  Placement = pos=(-2.3,0,0) rot=(0,0,1;0rad)
  Shapes = -> [Extrude028,Fusion004]
FEATURE [Sketcher::SketchObject] Sketch033
  FullyConstrained = true
  Placement = pos=(0,-14.3,2.37) rot=(-1,0,0;2.03453rad)
  sketch-geometry (4):
    g0: LineSegment StartX=0 StartY=1.5 StartZ=0 EndX=0 EndY=0 EndZ=0
    g1: LineSegment StartX=0 StartY=1.5 StartZ=0 EndX=5 EndY=1.5 EndZ=0
    g2: LineSegment StartX=5 StartY=1.5 StartZ=0 EndX=5 EndY=0 EndZ=0
    g3: LineSegment StartX=0 StartY=0 StartZ=0 EndX=5 EndY=0 EndZ=0
  constraints (13):
    c: Vertical(g0)
    c: Distance(g0) = 1.5
    c: Horizontal(g1)
    c: Distance(g1) = 5
    c: Coincident(g1,g0)
    c: Vertical(g2)
    c: Distance(g2) = 1.5
    c: Coincident(g2,g1)
    c: Block(g1)
    c: Block(g2)
    c: Block(g0)
    c: Coincident(g3,g0)
    c: Coincident(g3,g2)
FEATURE [Sketcher::SketchObject] Sketch034
  FullyConstrained = true
  Placement = pos=(0,-14.3,2.37) rot=(-1,0,0;2.03453rad)
  sketch-geometry (4):
    g0: LineSegment StartX=0 StartY=1.5 StartZ=0 EndX=4 EndY=1.5 EndZ=0
    g1: LineSegment StartX=4 StartY=1.5 StartZ=0 EndX=4 EndY=-2.5 EndZ=0
    g2: LineSegment StartX=4 StartY=-2.5 StartZ=0 EndX=0 EndY=-2.5 EndZ=0
    g3: LineSegment StartX=0 StartY=1.5 StartZ=0 EndX=0 EndY=-2.5 EndZ=0
  constraints (11):
    c: Horizontal(g0)
    c: Distance(g0) = 4
    c: Block(g0)
    c: Coincident(g1,g0)
    c: Vertical(g1)
    c: Distance(g1) = 4
    c: Coincident(g2,g1)
    c: Horizontal(g2)
    c: Distance(g2) = 4
    c: Coincident(g3,g0)
    c: Coincident(g3,g2)
FEATURE [Part::Extrusion] Extrude020  label="removeFromSolenoidDriverMainExtrude020"
  Base = -> Sketch020
  Dir = (0,0.894389,-0.447291)
  DirMode = 2
  FaceMakerClass = Part::FaceMakerBullseye
  LengthFwd = 3.1
  LengthRev = 0
  Placement = pos=(-4,-2.42,-0.8) rot=(0,0,1;0rad)
  Solid = true
  Symmetric = false
FEATURE [Part::Fillet] Fillet
  Base = -> Fusion003
  Edges = 1 edges r=10: [Edge5]
  Placement = pos=(-2,0,0) rot=(0,0,1;0rad)
FEATURE [Part::MultiFuse] Fusion001
  Placement = pos=(0,1.4,2.65) rot=(0,0,1;0rad)
  Shapes = -> [Extrude026,Extrude027]
FEATURE [Part::MultiFuse] Fusion002
  Shapes = -> [Extrude020,Fusion001]
FEATURE [Sketcher::SketchObject] Sketch035
  FullyConstrained = true
  Placement = pos=(0,-14.3,2.37) rot=(-1,0,0;2.03453rad)
  sketch-geometry (4):
    g0: LineSegment StartX=0 StartY=1.5 StartZ=0 EndX=0 EndY=0 EndZ=0
    g1: LineSegment StartX=0 StartY=1.5 StartZ=0 EndX=5 EndY=1.5 EndZ=0
    g2: LineSegment StartX=5 StartY=1.5 StartZ=0 EndX=5 EndY=0 EndZ=0
    g3: LineSegment StartX=0 StartY=0 StartZ=0 EndX=5 EndY=0 EndZ=0
  constraints (13):
    c: Vertical(g0)
    c: Distance(g0) = 1.5
    c: Horizontal(g1)
    c: Distance(g1) = 5
    c: Coincident(g1,g0)
    c: Vertical(g2)
    c: Distance(g2) = 1.5
    c: Coincident(g2,g1)
    c: Block(g1)
    c: Block(g2)
    c: Block(g0)
    c: Coincident(g3,g0)
    c: Coincident(g3,g2)
FEATURE [Sketcher::SketchObject] Sketch036
  FullyConstrained = true
  Placement = pos=(0,-14.3,2.37) rot=(-1,0,0;2.03453rad)
  sketch-geometry (4):
    g0: LineSegment StartX=0 StartY=1.5 StartZ=0 EndX=0 EndY=0 EndZ=0
    g1: LineSegment StartX=0 StartY=1.5 StartZ=0 EndX=5 EndY=1.5 EndZ=0
    g2: LineSegment StartX=5 StartY=1.5 StartZ=0 EndX=5 EndY=0 EndZ=0
    g3: LineSegment StartX=0 StartY=0 StartZ=0 EndX=5 EndY=0 EndZ=0
  constraints (13):
    c: Vertical(g0)
    c: Distance(g0) = 1.5
    c: Horizontal(g1)
    c: Distance(g1) = 5
    c: Coincident(g1,g0)
    c: Vertical(g2)
    c: Distance(g2) = 1.5
    c: Coincident(g2,g1)
    c: Block(g1)
    c: Block(g2)
    c: Block(g0)
    c: Coincident(g3,g0)
    c: Coincident(g3,g2)
FEATURE [Part::Extrusion] Extrude031  label="solenoidDriverBottomLipTopExtrude020"
  Base = -> Sketch035
  Dir = (0,0.894389,-0.447291)
  DirMode = 2
  FaceMakerClass = Part::FaceMakerBullseye
  LengthFwd = -6.5
  LengthRev = 0
  Placement = pos=(5,-14.15,19.65) rot=(1,0,0;1.5708rad)
  Solid = true
  Symmetric = false
FEATURE [Part::Extrusion] Extrude032  label="solenoidDriverBottomLipTopExtrude021"
  Base = -> Sketch036
  Dir = (0,0.894389,-0.447291)
  DirMode = 2
  FaceMakerClass = Part::FaceMakerBullseye
  LengthFwd = -6.5
  LengthRev = 0
  Placement = pos=(0,-14.15,19.65) rot=(1,0,0;1.5708rad)
  Solid = true
  Symmetric = false
FEATURE [Part::MultiFuse] Fusion009
  Placement = pos=(8,1.4,2.65) rot=(0,0,1;0rad)
  Shapes = -> [Extrude031,Extrude032]
FEATURE [Part::MultiFuse] Fusion010  label="removeFromSolenoidDriver"
  Shapes = -> [Fusion009,Fillet,Fusion002]
FEATURE [Sketcher::SketchObject] Sketch037
  FullyConstrained = true
  Placement = pos=(0,0,0) rot=(1,0,0;1.5708rad)
  sketch-geometry (4):
    g0: Circle CenterX=64.05 CenterY=16.5 CenterZ=0 NormalX=0 NormalY=0 NormalZ=1 AngleXU=0 Radius=2.7
    g1: Circle CenterX=64.05 CenterY=8.5 CenterZ=0 NormalX=0 NormalY=0 NormalZ=1 AngleXU=0 Radius=2.7
    g2: Circle CenterX=84.15 CenterY=8.5 CenterZ=0 NormalX=0 NormalY=0 NormalZ=1 AngleXU=0 Radius=2.7
    g3: Circle CenterX=84.15 CenterY=16.5 CenterZ=0 NormalX=0 NormalY=0 NormalZ=1 AngleXU=0 Radius=2.7
  constraints (4):
    c: Block(g2)
    c: Block(g3)
    c: Block(g0)
    c: Block(g1)
FEATURE [Part::Extrusion] Extrude033  label="removeFromMainBodyToCreateScrewHoleCounterSinks001"
  Base = -> Sketch037
  Dir = (0,-1,1.1e-15)
  DirMode = 2
  FaceMakerClass = Part::FaceMakerBullseye
  LengthFwd = 1.9
  LengthRev = 0
  Placement = pos=(0.8,0,0) rot=(0,0,1;0rad)
  Solid = true
  Symmetric = false
FEATURE [Part::MultiFuse] Fusion011  label="removeFromMainBodyToCreateScrewHoleCounterSinks001Fusion011"
  Shapes = -> [Extrude014,Extrude033]
FEATURE [Sketcher::SketchObject] Sketch038
  FullyConstrained = true
  Placement = pos=(0,-14.3,2.37) rot=(-1,0,0;2.03453rad)
  sketch-geometry (4):
    g0: LineSegment StartX=33.9 StartY=-9.7 StartZ=0 EndX=33.9 EndY=-1.5 EndZ=0
    g1: LineSegment StartX=33.9 StartY=-1.5 StartZ=0 EndX=44.5 EndY=-1.5 EndZ=0
    g2: LineSegment StartX=33.9 StartY=-9.7 StartZ=0 EndX=44.5 EndY=-9.7 EndZ=0
    g3: LineSegment StartX=44.5 StartY=-1.5 StartZ=0 EndX=44.5 EndY=-9.7 EndZ=0
  constraints (10):
    c: Vertical(g0)
    c: Coincident(g1,g0)
    c: Horizontal(g1)
    c: Block(g1)
    c: Block(g0)
    c: Coincident(g2,g0)
    c: Horizontal(g2)
    c: Coincident(g3,g1)
    c: Coincident(g3,g2)
    c: Vertical(g3)
FEATURE [Part::Extrusion] Extrude034
  Base = -> Sketch038
  Dir = (0,0.894389,-0.447291)
  DirMode = 2
  FaceMakerClass = Part::FaceMakerBullseye
  LengthFwd = 16
  LengthRev = 0
  Placement = pos=(0,-22,7) rot=(0,0,1;0rad)
  Solid = true
  Symmetric = false
FEATURE [Sketcher::SketchObject] Sketch039
  FullyConstrained = true
  Placement = pos=(0,-14.3,2.37) rot=(-1,0,0;2.03453rad)
  sketch-geometry (4):
    g0: LineSegment StartX=5.5 StartY=-7.7 StartZ=0 EndX=13.3 EndY=-7.7 EndZ=0
    g1: LineSegment StartX=13.3 StartY=-7.7 StartZ=0 EndX=13.3 EndY=-13.1 EndZ=0
    g2: LineSegment StartX=13.3 StartY=-13.1 StartZ=0 EndX=5.5 EndY=-13.1 EndZ=0
    g3: LineSegment StartX=5.5 StartY=-7.7 StartZ=0 EndX=5.5 EndY=-13.1 EndZ=0
  constraints (12):
    c: Horizontal(g0)
    c: Distance(g0) = 7.8
    c: Coincident(g1,g0)
    c: Vertical(g1)
    c: Distance(g1) = 5.4
    c: Coincident(g2,g1)
    c: Horizontal(g2)
    c: Vertical(g3)
    c: Coincident(g3,g2)
    c: Block(g0)
    c: Block(g2)
    c: Block(g3)
FEATURE [Part::Extrusion] Extrude035  label="removeToMakeHoleForConnectorExtrude035"
  Base = -> Sketch039
  Dir = (0,0.894389,-0.447291)
  DirMode = 2
  FaceMakerClass = Part::FaceMakerBullseye
  LengthFwd = 15
  LengthRev = 0
  Placement = pos=(-4,-22,9.6469) rot=(0,0,1;0rad)
  Solid = true
  Symmetric = false
FEATURE [App::MeasureDistance] Distance  label="Distance: 4.00 mm"
  Distance = 4.00184
  P1 = (119.349,-15.3,8)
  P2 = (123.351,-15.3,8)
FEATURE [App::MeasureDistance] Distance001  label="Distance: 3.80 mm"
  Distance = 3.8
  P1 = (119.45,-15.3,8)
  P2 = (123.25,-15.3,8)
FEATURE [Part::Fillet] Fillet015
  Base = -> Extrude009
  Edges = 1 edges r=1.59: [Edge7]
FEATURE [Part::Fillet] Fillet016
  Base = -> Extrude017
  Edges = 1 edges r=1.49: [Edge12]
FEATURE [Part::Fillet] Fillet017
  Base = -> Fillet016
  Edges = 1 edges r=1.45: [Edge8]
FEATURE [Part::MultiFuse] Fusion012  label="main"
  Shapes = -> [Extrude,Revolve,Extrude005,Fillet003,Fillet012,Fillet014,Extrude025,Fusion,Fillet015,Fillet017]
FEATURE [Part::Cut] Cut001
  Base = -> Fusion012
  Tool = -> Box003
FEATURE [Part::Cut] Cut002
  Base = -> Cut001
  Tool = -> Box002
FEATURE [Part::Cut] Cut003
  Base = -> Cut002
  Tool = -> Cut
FEATURE [Part::Cut] Cut004
  Base = -> Cut003
  Tool = -> Extrude019
FEATURE [Part::Cut] Cut005
  Base = -> Cut004
  Tool = -> Fusion011
FEATURE [Part::Cut] Cut006
  Base = -> Cut005
  Tool = -> Extrude004
FEATURE [Part::Cut] Cut007
  Base = -> Cut006
  Tool = -> Extrude015
FEATURE [Part::Cut] Cut008
  Base = -> Cut007
  Tool = -> Extrude008
FEATURE [Part::Cut] Cut009
  Base = -> Cut008
  Tool = -> Fusion010
FEATURE [App::MeasureDistance] Distance002  label="Distance: 2.05 mm"
  Distance = 2.05453
  P1 = (1.5,-23.0732,21.402)
  P2 = (6e-15,-23,20)
FEATURE [Part::Cut] Cut010
  Base = -> Cut009
  Tool = -> Extrude035
FEATURE [Part::Cut] Cut011
  Base = -> Cut010
  Tool = -> Extrude034
FEATURE [Part::Box] Box004  label="Cube004"
  AttacherType = Attacher::AttachEngine3D
  Height = 10
  Length = 200
  Placement = pos=(-30,0,0) rot=(0,0,1;0rad)
  Width = 10
FEATURE [Part::Fillet] Fillet020
  Base = -> Box004
  Edges = 1 edges r=3.6: [Edge12]
FEATURE [Part::Box] Box005  label="Cube005"
  AttacherType = Attacher::AttachEngine3D
  Height = 10
  Length = 198
  Placement = pos=(-30,0,0) rot=(0,0,1;0rad)
  Width = 10
FEATURE [Part::Cut] Cut012
  Base = -> Box005
  Tool = -> Fillet020
FEATURE [Part::Box] Box006  label="Cube006"
  AttacherType = Attacher::AttachEngine3D
  Height = 5
  Length = 200
  Placement = pos=(-30,6.4,10) rot=(1,0,0;0rad)
  Width = 5
FEATURE [Part::Box] Box007  label="Cube007"
  AttacherType = Attacher::AttachEngine3D
  Height = 5
  Length = 200
  Placement = pos=(-30,6.4,10) rot=(1,0,0;0.872665rad)
  Width = 5
FEATURE [Part::MultiFuse] Fusion013  label="removeFromMainFusion013"
  Placement = pos=(0,-10,10) rot=(0,0,1;0rad)
  Shapes = -> [Box007,Box006,Cut012]
FEATURE [Mesh::Feature] v0_98_Cut013  label="v0_98-Cut013"
FEATURE [App::MeasureDistance] Distance003  label="Distance: 7.18 mm"
  Distance = 7.17719
  P1 = (117.773,-15.3145,-2.4)
  P2 = (124.951,-15.2973,-2.4)
FEATURE [Sketcher::SketchObject] Sketch040
  FullyConstrained = true
  Placement = pos=(0,-14.3,2.37) rot=(-1,0,0;2.03453rad)
  sketch-geometry (4):
    g0: LineSegment StartX=0 StartY=1.5 StartZ=0 EndX=0 EndY=0 EndZ=0
    g1: LineSegment StartX=0 StartY=1.5 StartZ=0 EndX=5 EndY=1.5 EndZ=0
    g2: LineSegment StartX=5 StartY=1.5 StartZ=0 EndX=5 EndY=0 EndZ=0
    g3: LineSegment StartX=0 StartY=0 StartZ=0 EndX=5 EndY=0 EndZ=0
  constraints (13):
    c: Vertical(g0)
    c: Distance(g0) = 1.5
    c: Horizontal(g1)
    c: Distance(g1) = 5
    c: Coincident(g1,g0)
    c: Vertical(g2)
    c: Distance(g2) = 1.5
    c: Coincident(g2,g1)
    c: Block(g1)
    c: Block(g2)
    c: Block(g0)
    c: Coincident(g3,g0)
    c: Coincident(g3,g2)
FEATURE [Part::Extrusion] Extrude036
  Base = -> Sketch040
  Dir = (0,0.894389,-0.447291)
  DirMode = 2
  FaceMakerClass = Part::FaceMakerBullseye
  LengthFwd = 1.4
  LengthRev = 0
  Placement = pos=(0,8.25,17.58) rot=(0,0,1;0rad)
  Solid = true
  Symmetric = false
FEATURE [Sketcher::SketchObject] Sketch041
  FullyConstrained = true
  Placement = pos=(0,-14.3,2.37) rot=(-1,0,0;2.03453rad)
  sketch-geometry (4):
    g0: LineSegment StartX=0 StartY=1.5 StartZ=0 EndX=0 EndY=0 EndZ=0
    g1: LineSegment StartX=0 StartY=1.5 StartZ=0 EndX=5 EndY=1.5 EndZ=0
    g2: LineSegment StartX=5 StartY=1.5 StartZ=0 EndX=5 EndY=0 EndZ=0
    g3: LineSegment StartX=0 StartY=0 StartZ=0 EndX=5 EndY=0 EndZ=0
  constraints (13):
    c: Vertical(g0)
    c: Distance(g0) = 1.5
    c: Horizontal(g1)
    c: Distance(g1) = 5
    c: Coincident(g1,g0)
    c: Vertical(g2)
    c: Distance(g2) = 1.5
    c: Coincident(g2,g1)
    c: Block(g1)
    c: Block(g2)
    c: Block(g0)
    c: Coincident(g3,g0)
    c: Coincident(g3,g2)
FEATURE [Part::Extrusion] Extrude037
  Base = -> Sketch041
  Dir = (0,0.894389,-0.447291)
  DirMode = 2
  FaceMakerClass = Part::FaceMakerBullseye
  LengthFwd = 1.4
  LengthRev = 0
  Placement = pos=(0,6.11,13.33) rot=(0,0,1;0rad)
  Solid = true
  Symmetric = false
FEATURE [Part::MultiFuse] Fusion014  label="screwSpacerFusion014"
  Shapes = -> [Extrude037,Extrude036]
FEATURE [Sketcher::SketchObject] Sketch042
  FullyConstrained = true
  Placement = pos=(0,-14.3,2.37) rot=(-1,0,0;2.03453rad)
  sketch-geometry (4):
    g0: LineSegment StartX=0 StartY=1.5 StartZ=0 EndX=0 EndY=0 EndZ=0
    g1: LineSegment StartX=0 StartY=1.5 StartZ=0 EndX=5 EndY=1.5 EndZ=0
    g2: LineSegment StartX=5 StartY=1.5 StartZ=0 EndX=5 EndY=0 EndZ=0
    g3: LineSegment StartX=0 StartY=0 StartZ=0 EndX=5 EndY=0 EndZ=0
  constraints (13):
    c: Vertical(g0)
    c: Distance(g0) = 1.5
    c: Horizontal(g1)
    c: Distance(g1) = 5
    c: Coincident(g1,g0)
    c: Vertical(g2)
    c: Distance(g2) = 1.5
    c: Coincident(g2,g1)
    c: Block(g1)
    c: Block(g2)
    c: Block(g0)
    c: Coincident(g3,g0)
    c: Coincident(g3,g2)
FEATURE [Part::Extrusion] Extrude038
  Base = -> Sketch042
  Dir = (0,0.894389,-0.447291)
  DirMode = 2
  FaceMakerClass = Part::FaceMakerBullseye
  LengthFwd = 1.4
  LengthRev = 0
  Placement = pos=(0,8.459,18) rot=(0,0,1;0rad)
  Solid = true
  Symmetric = false
FEATURE [Part::MultiFuse] Fusion015  label="screwSpacerFusion014Fusion015"
  Placement = pos=(0,0.35,-0.18) rot=(0,0,1;0rad)
  Shapes = -> [Extrude038,Fusion014]
FEATURE [Part::Cylinder] Cylinder
  Angle = 360
  AttacherType = Attacher::AttachEngine3D
  Height = 10
  Placement = pos=(0,10,0) rot=(0,0,1;0rad)
  Radius = 1.5
FEATURE [Part::Cylinder] Cylinder001
  Angle = 360
  AttacherType = Attacher::AttachEngine3D
  Height = 10
  Placement = pos=(3,10,0) rot=(0,0,1;0rad)
  Radius = 1.5
FEATURE [Part::Box] Box008  label="Cube008"
  AttacherType = Attacher::AttachEngine3D
  Height = 10
  Length = 3
  Placement = pos=(0,8.5,0) rot=(0,0,1;0rad)
  Width = 3
FEATURE [Part::MultiFuse] Fusion016  label="holeForWireFusion016"
  Shapes = -> [Cylinder001,Box008,Cylinder]
FEATURE [Part::Box] Box009  label="Cube009"
  AttacherType = Attacher::AttachEngine3D
  Height = 10
  Length = 3
  Placement = pos=(0,8.5,0) rot=(0,0,1;0rad)
  Width = 3
FEATURE [Part::Cylinder] Cylinder002
  Angle = 360
  AttacherType = Attacher::AttachEngine3D
  Height = 10
  Placement = pos=(0,10,0) rot=(0,0,1;0rad)
  Radius = 1.5
FEATURE [Part::Cylinder] Cylinder003
  Angle = 360
  AttacherType = Attacher::AttachEngine3D
  Height = 10
  Placement = pos=(3,10,0) rot=(0,0,1;0rad)
  Radius = 1.5
FEATURE [Part::MultiFuse] Fusion017  label="holeForWireFusion017"
  Placement = pos=(0,0,10) rot=(0,0,1;0rad)
  Shapes = -> [Cylinder003,Box009,Cylinder002]
FEATURE [Part::MultiFuse] Fusion018  label="holeForWireFusion018"
  Placement = pos=(0,0,0) rot=(0,-1,0;1.5708rad)
  Shapes = -> [Fusion017,Fusion016]
FEATURE [Part::Box] Box010  label="Cube010"
  AttacherType = Attacher::AttachEngine3D
  Height = 0.1
  Length = 0.1
  Placement = pos=(-2,10,0) rot=(0,0.995037,0.099504;0rad)
  Width = 0.1
FEATURE [Part::MultiFuse] Fusion019
  Placement = pos=(0,10,0) rot=(1,0,0;1.5708rad)
  Shapes = -> [Box010,Fusion018]
FEATURE [Part::Box] Box011  label="Cube011"
  AttacherType = Attacher::AttachEngine3D
  Height = 0.1
  Length = 1.1
  Placement = pos=(-2,10,10) rot=(0,0.995037,0.099504;0rad)
  Width = 0.1
FEATURE [Part::MultiFuse] Fusion020
  Placement = pos=(0,0,0) rot=(0,1,0;0.349066rad)
  Shapes = -> [Box011,Fusion019]
FEATURE [Part::Box] Box012  label="Cube012"
  AttacherType = Attacher::AttachEngine3D
  Height = 0.1
  Length = 1.1
  Placement = pos=(-2,10,10) rot=(0,0.995037,0.099504;0rad)
  Width = 0.1
FEATURE [Part::MultiFuse] Fusion021
  Placement = pos=(0,30,0) rot=(0,0,1;3.63029rad)
  Shapes = -> [Box012,Fusion020]
FEATURE [Part::Box] Box013  label="Cube013"
  AttacherType = Attacher::AttachEngine3D
  Height = 0.1
  Length = 1.1
  Placement = pos=(2,19,10) rot=(0,0.995037,0.099504;0rad)
  Width = 0.1
FEATURE [Part::MultiFuse] Fusion022  label="holeForWire"
  Placement = pos=(15,-49.8,-8.2) rot=(0,0,1;0rad)
  Shapes = -> [Box013,Fusion021]
FEATURE [Part::Cut] Cut013
  Base = -> Cut011
  Tool = -> Fusion013
FEATURE [Part::Cut] Cut014
  Base = -> Cut013
  Tool = -> Fusion022
FEATURE [Sketcher::SketchObject] Sketch043
  FullyConstrained = true
  MapMode = 4
  Placement = pos=(0,0,0) rot=(0.57735,0.57735,0.57735;2.0944rad)
  Support = -> [Cut014]
  sketch-geometry (14):
    g0: LineSegment StartX=6.08745 StartY=-4.11588 StartZ=0 EndX=6.08745 EndY=-2.11589 EndZ=0
    g1: LineSegment StartX=3.58745 StartY=2.38411 StartZ=0 EndX=3.58745 EndY=4.38411 EndZ=0
    g2: LineSegment StartX=8.08745 StartY=1.38411 StartZ=0 EndX=8.08745 EndY=-1.11589 EndZ=0
    g3: ArcOfCircle CenterX=7.08745 CenterY=-1.11589 CenterZ=0 NormalX=0 NormalY=0 NormalZ=1 AngleXU=0 Radius=1 StartAngle=4.71239 EndAngle=6.28319
    g4: LineSegment StartX=6.08745 StartY=-2.11589 StartZ=0 EndX=7.08745 EndY=-2.11589 EndZ=0
    g5: LineSegment StartX=6.08745 StartY=-4.11588 StartZ=0 EndX=7.08745 EndY=-4.11588 EndZ=0
    g6: ArcOfCircle CenterX=7.08745 CenterY=-1.11589 CenterZ=0 NormalX=0 NormalY=0 NormalZ=1 AngleXU=0 Radius=3 StartAngle=4.71239 EndAngle=6.28319
    g7: ArcOfCircle CenterX=7.08745 CenterY=1.38411 CenterZ=0 NormalX=0 NormalY=0 NormalZ=1 AngleXU=0 Radius=1 StartAngle=5.35e-14 EndAngle=1.5708
    g8: LineSegment StartX=3.58745 StartY=4.38411 StartZ=0 EndX=7.08745 EndY=4.38411 EndZ=0
    g9: LineSegment StartX=10.0875 StartY=-1.11588 StartZ=0 EndX=10.0875 EndY=1.38411 EndZ=0
    g10: ArcOfCircle CenterX=7.08745 CenterY=1.38411 CenterZ=0 NormalX=0 NormalY=0 NormalZ=1 AngleXU=0 Radius=3 StartAngle=3.57e-14 EndAngle=1.5708
    g11: LineSegment StartX=3.58745 StartY=2.38411 StartZ=0 EndX=3.58745 EndY=1.38411 EndZ=0
    g12: ArcOfCircle CenterX=4.58745 CenterY=1.38412 CenterZ=0 NormalX=0 NormalY=0 NormalZ=1 AngleXU=0 Radius=1 StartAngle=1.57081 EndAngle=3.14159
    g13: LineSegment StartX=4.58744 StartY=2.38411 StartZ=0 EndX=7.08745 EndY=2.38411 EndZ=0
  constraints (33):
    c: Vertical(g0)
    c: Vertical(g1)
    c: Distance(g1) = 2
    c: Block(g0)
    c: Block(g2)
    c: Coincident(g3,g2)
    c: Coincident(g4,g0)
    c: Coincident(g4,g3)
    c: Horizontal(g4)
    c: Block(g3)
    c: Coincident(g5,g0)
    c: Horizontal(g5)
    c: Coincident(g6,g3)
    c: Block(g6)
    c: Block(g5)
    c: Coincident(g7,g2)
    c: Block(g7)
    c: Coincident(g8,g1)
    c: Coincident(g9,g6)
    c: Vertical(g9)
    c: Coincident(g10,g7)
    c: Block(g10)
    c: Block(g8)
    c: Block(g9)
    c: Coincident(g11,g1)
    c: Vertical(g11)
    c: Distance(g11) = 1
    c: Coincident(g12,g11)
    c: Coincident(g13,g12)
    c: Coincident(g13,g7)
    c: Horizontal(g13)
    c: Block(g13)
    c: Block(g12)
FEATURE [Sketcher::SketchObject] Sketch044
  FullyConstrained = true
  MapMode = 4
  Placement = pos=(0,0,0) rot=(0.57735,0.57735,0.57735;2.0944rad)
  Support = -> [Cut014]
  sketch-geometry (14):
    g0: LineSegment StartX=6.08745 StartY=-4.11588 StartZ=0 EndX=6.08745 EndY=-2.11589 EndZ=0
    g1: LineSegment StartX=8.08745 StartY=1.38411 StartZ=0 EndX=8.08745 EndY=-1.11589 EndZ=0
    g2: ArcOfCircle CenterX=7.08745 CenterY=-1.11589 CenterZ=0 NormalX=0 NormalY=0 NormalZ=1 AngleXU=0 Radius=1 StartAngle=4.71239 EndAngle=6.28319
    g3: LineSegment StartX=6.08745 StartY=-2.11589 StartZ=0 EndX=7.08745 EndY=-2.11589 EndZ=0
    g4: LineSegment StartX=6.08745 StartY=-4.11588 StartZ=0 EndX=7.08745 EndY=-4.11588 EndZ=0
    g5: ArcOfCircle CenterX=7.08745 CenterY=-1.11589 CenterZ=0 NormalX=0 NormalY=0 NormalZ=1 AngleXU=0 Radius=3 StartAngle=4.71239 EndAngle=6.28319
    g6: ArcOfCircle CenterX=7.08745 CenterY=1.38411 CenterZ=0 NormalX=0 NormalY=0 NormalZ=1 AngleXU=0 Radius=1 StartAngle=5.35e-14 EndAngle=1.5708
    g7: LineSegment StartX=10.0875 StartY=-1.11588 StartZ=0 EndX=10.0875 EndY=1.38411 EndZ=0
    g8: ArcOfCircle CenterX=7.08745 CenterY=1.38411 CenterZ=0 NormalX=0 NormalY=0 NormalZ=1 AngleXU=0 Radius=3 StartAngle=3.57e-14 EndAngle=1.5708
    g9: ArcOfCircle CenterX=4.58745 CenterY=1.38412 CenterZ=0 NormalX=0 NormalY=0 NormalZ=1 AngleXU=0 Radius=1 StartAngle=1.57081 EndAngle=3.14159
    g10: LineSegment StartX=4.58744 StartY=2.38411 StartZ=0 EndX=7.08745 EndY=2.38411 EndZ=0
    g11: LineSegment StartX=4.58745 StartY=4.38411 StartZ=0 EndX=7.08745 EndY=4.38411 EndZ=0
    g12: ArcOfCircle CenterX=4.58745 CenterY=5.38411 CenterZ=0 NormalX=0 NormalY=0 NormalZ=1 AngleXU=0 Radius=1 StartAngle=3.14159 EndAngle=4.71239
    g13: LineSegment StartX=3.58745 StartY=5.38411 StartZ=0 EndX=3.58745 EndY=1.38411 EndZ=0
  constraints (33):
    c: Vertical(g0)
    c: Block(g0)
    c: Block(g1)
    c: Coincident(g2,g1)
    c: Coincident(g3,g0)
    c: Coincident(g3,g2)
    c: Horizontal(g3)
    c: Block(g2)
    c: Coincident(g4,g0)
    c: Horizontal(g4)
    c: Coincident(g5,g2)
    c: Block(g5)
    c: Block(g4)
    c: Coincident(g6,g1)
    c: Block(g6)
    c: Coincident(g7,g5)
    c: Vertical(g7)
    c: Coincident(g8,g6)
    c: Block(g8)
    c: Block(g7)
    c: Coincident(g10,g9)
    c: Coincident(g10,g6)
    c: Horizontal(g10)
    c: Block(g10)
    c: Block(g9)
    c: Coincident(g11,g8)
    c: Horizontal(g11)
    c: Block(g12)
    c: Block(g11)
    c: Coincident(g13,g12)
    c: Coincident(g13,g9)
    c: Vertical(g13)
    c: Tangent(g13,g9)
FEATURE [Part::Extrusion] Extrude039
  Base = -> Sketch044
  Dir = (1,0,0)
  DirMode = 2
  FaceMakerClass = Part::FaceMakerBullseye
  LengthFwd = 10
  LengthRev = 0
  Placement = pos=(8,-22.615,4.115) rot=(0,0,1;3.14159rad)
  Solid = true
  Symmetric = false
FEATURE [App::MeasureDistance] Distance004  label="Distance: 42.16 mm"
  Distance = 42.1607
  P1 = (14.6786,-26.2,1.24491)
  P2 = (-27.4815,-26.2,1.03853)
FEATURE [Sketcher::SketchObject] Sketch045
  FullyConstrained = true
  MapMode = 4
  Placement = pos=(0,0,0) rot=(0.57735,0.57735,0.57735;2.0944rad)
  Support = -> [Cut014]
  sketch-geometry (14):
    g0: LineSegment StartX=6.08745 StartY=-4.11588 StartZ=0 EndX=6.08745 EndY=-2.11589 EndZ=0
    g1: LineSegment StartX=8.08745 StartY=1.38411 StartZ=0 EndX=8.08745 EndY=-1.11589 EndZ=0
    g2: ArcOfCircle CenterX=7.08745 CenterY=-1.11589 CenterZ=0 NormalX=0 NormalY=0 NormalZ=1 AngleXU=0 Radius=1 StartAngle=4.71239 EndAngle=6.28319
    g3: LineSegment StartX=6.08745 StartY=-2.11589 StartZ=0 EndX=7.08745 EndY=-2.11589 EndZ=0
    g4: LineSegment StartX=6.08745 StartY=-4.11588 StartZ=0 EndX=7.08745 EndY=-4.11588 EndZ=0
    g5: ArcOfCircle CenterX=7.08745 CenterY=-1.11589 CenterZ=0 NormalX=0 NormalY=0 NormalZ=1 AngleXU=0 Radius=3 StartAngle=4.71239 EndAngle=6.28319
    g6: ArcOfCircle CenterX=7.08745 CenterY=1.38411 CenterZ=0 NormalX=0 NormalY=0 NormalZ=1 AngleXU=0 Radius=1 StartAngle=5.35e-14 EndAngle=1.5708
    g7: LineSegment StartX=10.0875 StartY=-1.11588 StartZ=0 EndX=10.0875 EndY=1.38411 EndZ=0
    g8: ArcOfCircle CenterX=7.08745 CenterY=1.38411 CenterZ=0 NormalX=0 NormalY=0 NormalZ=1 AngleXU=0 Radius=3 StartAngle=3.57e-14 EndAngle=1.5708
    g9: ArcOfCircle CenterX=4.58745 CenterY=1.38412 CenterZ=0 NormalX=0 NormalY=0 NormalZ=1 AngleXU=0 Radius=1 StartAngle=1.57081 EndAngle=3.14159
    g10: LineSegment StartX=4.58744 StartY=2.38411 StartZ=0 EndX=7.08745 EndY=2.38411 EndZ=0
    g11: LineSegment StartX=4.58745 StartY=4.38411 StartZ=0 EndX=7.08745 EndY=4.38411 EndZ=0
    g12: ArcOfCircle CenterX=4.58745 CenterY=5.38411 CenterZ=0 NormalX=0 NormalY=0 NormalZ=1 AngleXU=0 Radius=1 StartAngle=3.14159 EndAngle=4.71239
    g13: LineSegment StartX=3.58745 StartY=5.38411 StartZ=0 EndX=3.58745 EndY=1.38411 EndZ=0
  constraints (33):
    c: Vertical(g0)
    c: Block(g0)
    c: Block(g1)
    c: Coincident(g2,g1)
    c: Coincident(g3,g0)
    c: Coincident(g3,g2)
    c: Horizontal(g3)
    c: Block(g2)
    c: Coincident(g4,g0)
    c: Horizontal(g4)
    c: Coincident(g5,g2)
    c: Block(g5)
    c: Block(g4)
    c: Coincident(g6,g1)
    c: Block(g6)
    c: Coincident(g7,g5)
    c: Vertical(g7)
    c: Coincident(g8,g6)
    c: Block(g8)
    c: Block(g7)
    c: Coincident(g10,g9)
    c: Coincident(g10,g6)
    c: Horizontal(g10)
    c: Block(g10)
    c: Block(g9)
    c: Coincident(g11,g8)
    c: Horizontal(g11)
    c: Block(g12)
    c: Block(g11)
    c: Coincident(g13,g12)
    c: Coincident(g13,g9)
    c: Vertical(g13)
    c: Tangent(g13,g9)
FEATURE [Part::Extrusion] Extrude040
  Base = -> Sketch045
  Dir = (1,0,0)
  DirMode = 2
  FaceMakerClass = Part::FaceMakerBullseye
  LengthFwd = 10
  LengthRev = 0
  Placement = pos=(-17.5,-22.615,4.115) rot=(0,0,1;3.14159rad)
  Solid = true
  Symmetric = false
FEATURE [Sketcher::SketchObject] Sketch046
  FullyConstrained = true
  MapMode = 4
  Placement = pos=(0,0,0) rot=(0.57735,0.57735,0.57735;2.0944rad)
  Support = -> [Cut014]
  sketch-geometry (14):
    g0: LineSegment StartX=6.08745 StartY=-4.11588 StartZ=0 EndX=6.08745 EndY=-2.11589 EndZ=0
    g1: LineSegment StartX=8.08745 StartY=1.38411 StartZ=0 EndX=8.08745 EndY=-1.11589 EndZ=0
    g2: ArcOfCircle CenterX=7.08745 CenterY=-1.11589 CenterZ=0 NormalX=0 NormalY=0 NormalZ=1 AngleXU=0 Radius=1 StartAngle=4.71239 EndAngle=6.28319
    g3: LineSegment StartX=6.08745 StartY=-2.11589 StartZ=0 EndX=7.08745 EndY=-2.11589 EndZ=0
    g4: LineSegment StartX=6.08745 StartY=-4.11588 StartZ=0 EndX=7.08745 EndY=-4.11588 EndZ=0
    g5: ArcOfCircle CenterX=7.08745 CenterY=-1.11589 CenterZ=0 NormalX=0 NormalY=0 NormalZ=1 AngleXU=0 Radius=3 StartAngle=4.71239 EndAngle=6.28319
    g6: ArcOfCircle CenterX=7.08745 CenterY=1.38411 CenterZ=0 NormalX=0 NormalY=0 NormalZ=1 AngleXU=0 Radius=1 StartAngle=5.35e-14 EndAngle=1.5708
    g7: LineSegment StartX=10.0875 StartY=-1.11588 StartZ=0 EndX=10.0875 EndY=1.38411 EndZ=0
    g8: ArcOfCircle CenterX=7.08745 CenterY=1.38411 CenterZ=0 NormalX=0 NormalY=0 NormalZ=1 AngleXU=0 Radius=3 StartAngle=3.57e-14 EndAngle=1.5708
    g9: ArcOfCircle CenterX=4.58745 CenterY=1.38412 CenterZ=0 NormalX=0 NormalY=0 NormalZ=1 AngleXU=0 Radius=1 StartAngle=1.57081 EndAngle=3.14159
    g10: LineSegment StartX=4.58744 StartY=2.38411 StartZ=0 EndX=7.08745 EndY=2.38411 EndZ=0
    g11: LineSegment StartX=4.58745 StartY=4.38411 StartZ=0 EndX=7.08745 EndY=4.38411 EndZ=0
    g12: ArcOfCircle CenterX=4.58745 CenterY=5.38411 CenterZ=0 NormalX=0 NormalY=0 NormalZ=1 AngleXU=0 Radius=1 StartAngle=3.14159 EndAngle=4.71239
    g13: LineSegment StartX=3.58745 StartY=5.38411 StartZ=0 EndX=3.58745 EndY=1.38411 EndZ=0
  constraints (33):
    c: Vertical(g0)
    c: Block(g0)
    c: Block(g1)
    c: Coincident(g2,g1)
    c: Coincident(g3,g0)
    c: Coincident(g3,g2)
    c: Horizontal(g3)
    c: Block(g2)
    c: Coincident(g4,g0)
    c: Horizontal(g4)
    c: Coincident(g5,g2)
    c: Block(g5)
    c: Block(g4)
    c: Coincident(g6,g1)
    c: Block(g6)
    c: Coincident(g7,g5)
    c: Vertical(g7)
    c: Coincident(g8,g6)
    c: Block(g8)
    c: Block(g7)
    c: Coincident(g10,g9)
    c: Coincident(g10,g6)
    c: Horizontal(g10)
    c: Block(g10)
    c: Block(g9)
    c: Coincident(g11,g8)
    c: Horizontal(g11)
    c: Block(g12)
    c: Block(g11)
    c: Coincident(g13,g12)
    c: Coincident(g13,g9)
    c: Vertical(g13)
    c: Tangent(g13,g9)
FEATURE [Sketcher::SketchObject] Sketch047
  FullyConstrained = true
  MapMode = 4
  Placement = pos=(0,0,0) rot=(0.57735,0.57735,0.57735;2.0944rad)
  Support = -> [Cut014]
  sketch-geometry (14):
    g0: LineSegment StartX=6.08745 StartY=-4.11588 StartZ=0 EndX=6.08745 EndY=-2.11589 EndZ=0
    g1: LineSegment StartX=8.08745 StartY=1.38411 StartZ=0 EndX=8.08745 EndY=-1.11589 EndZ=0
    g2: ArcOfCircle CenterX=7.08745 CenterY=-1.11589 CenterZ=0 NormalX=0 NormalY=0 NormalZ=1 AngleXU=0 Radius=1 StartAngle=4.71239 EndAngle=6.28319
    g3: LineSegment StartX=6.08745 StartY=-2.11589 StartZ=0 EndX=7.08745 EndY=-2.11589 EndZ=0
    g4: LineSegment StartX=6.08745 StartY=-4.11588 StartZ=0 EndX=7.08745 EndY=-4.11588 EndZ=0
    g5: ArcOfCircle CenterX=7.08745 CenterY=-1.11589 CenterZ=0 NormalX=0 NormalY=0 NormalZ=1 AngleXU=0 Radius=3 StartAngle=4.71239 EndAngle=6.28319
    g6: ArcOfCircle CenterX=7.08745 CenterY=1.38411 CenterZ=0 NormalX=0 NormalY=0 NormalZ=1 AngleXU=0 Radius=1 StartAngle=5.35e-14 EndAngle=1.5708
    g7: LineSegment StartX=10.0875 StartY=-1.11588 StartZ=0 EndX=10.0875 EndY=1.38411 EndZ=0
    g8: ArcOfCircle CenterX=7.08745 CenterY=1.38411 CenterZ=0 NormalX=0 NormalY=0 NormalZ=1 AngleXU=0 Radius=3 StartAngle=3.57e-14 EndAngle=1.5708
    g9: ArcOfCircle CenterX=4.58745 CenterY=1.38412 CenterZ=0 NormalX=0 NormalY=0 NormalZ=1 AngleXU=0 Radius=1 StartAngle=1.57081 EndAngle=3.14159
    g10: LineSegment StartX=4.58744 StartY=2.38411 StartZ=0 EndX=7.08745 EndY=2.38411 EndZ=0
    g11: LineSegment StartX=4.58745 StartY=4.38411 StartZ=0 EndX=7.08745 EndY=4.38411 EndZ=0
    g12: ArcOfCircle CenterX=4.58745 CenterY=5.38411 CenterZ=0 NormalX=0 NormalY=0 NormalZ=1 AngleXU=0 Radius=1 StartAngle=3.14159 EndAngle=4.71239
    g13: LineSegment StartX=3.58745 StartY=5.38411 StartZ=0 EndX=3.58745 EndY=1.38411 EndZ=0
  constraints (33):
    c: Vertical(g0)
    c: Block(g0)
    c: Block(g1)
    c: Coincident(g2,g1)
    c: Coincident(g3,g0)
    c: Coincident(g3,g2)
    c: Horizontal(g3)
    c: Block(g2)
    c: Coincident(g4,g0)
    c: Horizontal(g4)
    c: Coincident(g5,g2)
    c: Block(g5)
    c: Block(g4)
    c: Coincident(g6,g1)
    c: Block(g6)
    c: Coincident(g7,g5)
    c: Vertical(g7)
    c: Coincident(g8,g6)
    c: Block(g8)
    c: Block(g7)
    c: Coincident(g10,g9)
    c: Coincident(g10,g6)
    c: Horizontal(g10)
    c: Block(g10)
    c: Block(g9)
    c: Coincident(g11,g8)
    c: Horizontal(g11)
    c: Block(g12)
    c: Block(g11)
    c: Coincident(g13,g12)
    c: Coincident(g13,g9)
    c: Vertical(g13)
    c: Tangent(g13,g9)
FEATURE [Sketcher::SketchObject] Sketch048
  FullyConstrained = true
  MapMode = 4
  Placement = pos=(0,0,0) rot=(0.57735,0.57735,0.57735;2.0944rad)
  Support = -> [Cut014]
  sketch-geometry (14):
    g0: LineSegment StartX=6.08745 StartY=-4.11588 StartZ=0 EndX=6.08745 EndY=-2.11589 EndZ=0
    g1: LineSegment StartX=8.08745 StartY=1.38411 StartZ=0 EndX=8.08745 EndY=-1.11589 EndZ=0
    g2: ArcOfCircle CenterX=7.08745 CenterY=-1.11589 CenterZ=0 NormalX=0 NormalY=0 NormalZ=1 AngleXU=0 Radius=1 StartAngle=4.71239 EndAngle=6.28319
    g3: LineSegment StartX=6.08745 StartY=-2.11589 StartZ=0 EndX=7.08745 EndY=-2.11589 EndZ=0
    g4: LineSegment StartX=6.08745 StartY=-4.11588 StartZ=0 EndX=7.08745 EndY=-4.11588 EndZ=0
    g5: ArcOfCircle CenterX=7.08745 CenterY=-1.11589 CenterZ=0 NormalX=0 NormalY=0 NormalZ=1 AngleXU=0 Radius=3 StartAngle=4.71239 EndAngle=6.28319
    g6: ArcOfCircle CenterX=7.08745 CenterY=1.38411 CenterZ=0 NormalX=0 NormalY=0 NormalZ=1 AngleXU=0 Radius=1 StartAngle=5.35e-14 EndAngle=1.5708
    g7: LineSegment StartX=10.0875 StartY=-1.11588 StartZ=0 EndX=10.0875 EndY=1.38411 EndZ=0
    g8: ArcOfCircle CenterX=7.08745 CenterY=1.38411 CenterZ=0 NormalX=0 NormalY=0 NormalZ=1 AngleXU=0 Radius=3 StartAngle=3.57e-14 EndAngle=1.5708
    g9: ArcOfCircle CenterX=4.58745 CenterY=1.38412 CenterZ=0 NormalX=0 NormalY=0 NormalZ=1 AngleXU=0 Radius=1 StartAngle=1.57081 EndAngle=3.14159
    g10: LineSegment StartX=4.58744 StartY=2.38411 StartZ=0 EndX=7.08745 EndY=2.38411 EndZ=0
    g11: LineSegment StartX=4.58745 StartY=4.38411 StartZ=0 EndX=7.08745 EndY=4.38411 EndZ=0
    g12: ArcOfCircle CenterX=4.58745 CenterY=5.38411 CenterZ=0 NormalX=0 NormalY=0 NormalZ=1 AngleXU=0 Radius=1 StartAngle=3.14159 EndAngle=4.71239
    g13: LineSegment StartX=3.58745 StartY=5.38411 StartZ=0 EndX=3.58745 EndY=1.38411 EndZ=0
  constraints (33):
    c: Vertical(g0)
    c: Block(g0)
    c: Block(g1)
    c: Coincident(g2,g1)
    c: Coincident(g3,g0)
    c: Coincident(g3,g2)
    c: Horizontal(g3)
    c: Block(g2)
    c: Coincident(g4,g0)
    c: Horizontal(g4)
    c: Coincident(g5,g2)
    c: Block(g5)
    c: Block(g4)
    c: Coincident(g6,g1)
    c: Block(g6)
    c: Coincident(g7,g5)
    c: Vertical(g7)
    c: Coincident(g8,g6)
    c: Block(g8)
    c: Block(g7)
    c: Coincident(g10,g9)
    c: Coincident(g10,g6)
    c: Horizontal(g10)
    c: Block(g10)
    c: Block(g9)
    c: Coincident(g11,g8)
    c: Horizontal(g11)
    c: Block(g12)
    c: Block(g11)
    c: Coincident(g13,g12)
    c: Coincident(g13,g9)
    c: Vertical(g13)
    c: Tangent(g13,g9)
FEATURE [Sketcher::SketchObject] Sketch049
  FullyConstrained = true
  MapMode = 4
  Placement = pos=(0,0,0) rot=(0.57735,0.57735,0.57735;2.0944rad)
  Support = -> [Cut014]
  sketch-geometry (14):
    g0: LineSegment StartX=6.08745 StartY=-4.11588 StartZ=0 EndX=6.08745 EndY=-2.11589 EndZ=0
    g1: LineSegment StartX=8.08745 StartY=1.38411 StartZ=0 EndX=8.08745 EndY=-1.11589 EndZ=0
    g2: ArcOfCircle CenterX=7.08745 CenterY=-1.11589 CenterZ=0 NormalX=0 NormalY=0 NormalZ=1 AngleXU=0 Radius=1 StartAngle=4.71239 EndAngle=6.28319
    g3: LineSegment StartX=6.08745 StartY=-2.11589 StartZ=0 EndX=7.08745 EndY=-2.11589 EndZ=0
    g4: LineSegment StartX=6.08745 StartY=-4.11588 StartZ=0 EndX=7.08745 EndY=-4.11588 EndZ=0
    g5: ArcOfCircle CenterX=7.08745 CenterY=-1.11589 CenterZ=0 NormalX=0 NormalY=0 NormalZ=1 AngleXU=0 Radius=3 StartAngle=4.71239 EndAngle=6.28319
    g6: ArcOfCircle CenterX=7.08745 CenterY=1.38411 CenterZ=0 NormalX=0 NormalY=0 NormalZ=1 AngleXU=0 Radius=1 StartAngle=5.35e-14 EndAngle=1.5708
    g7: LineSegment StartX=10.0875 StartY=-1.11588 StartZ=0 EndX=10.0875 EndY=1.38411 EndZ=0
    g8: ArcOfCircle CenterX=7.08745 CenterY=1.38411 CenterZ=0 NormalX=0 NormalY=0 NormalZ=1 AngleXU=0 Radius=3 StartAngle=3.57e-14 EndAngle=1.5708
    g9: ArcOfCircle CenterX=4.58745 CenterY=1.38412 CenterZ=0 NormalX=0 NormalY=0 NormalZ=1 AngleXU=0 Radius=1 StartAngle=1.57081 EndAngle=3.14159
    g10: LineSegment StartX=4.58744 StartY=2.38411 StartZ=0 EndX=7.08745 EndY=2.38411 EndZ=0
    g11: LineSegment StartX=4.58745 StartY=4.38411 StartZ=0 EndX=7.08745 EndY=4.38411 EndZ=0
    g12: ArcOfCircle CenterX=4.58745 CenterY=5.38411 CenterZ=0 NormalX=0 NormalY=0 NormalZ=1 AngleXU=0 Radius=1 StartAngle=3.14159 EndAngle=4.71239
    g13: LineSegment StartX=3.58745 StartY=5.38411 StartZ=0 EndX=3.58745 EndY=1.38411 EndZ=0
  constraints (33):
    c: Vertical(g0)
    c: Block(g0)
    c: Block(g1)
    c: Coincident(g2,g1)
    c: Coincident(g3,g0)
    c: Coincident(g3,g2)
    c: Horizontal(g3)
    c: Block(g2)
    c: Coincident(g4,g0)
    c: Horizontal(g4)
    c: Coincident(g5,g2)
    c: Block(g5)
    c: Block(g4)
    c: Coincident(g6,g1)
    c: Block(g6)
    c: Coincident(g7,g5)
    c: Vertical(g7)
    c: Coincident(g8,g6)
    c: Block(g8)
    c: Block(g7)
    c: Coincident(g10,g9)
    c: Coincident(g10,g6)
    c: Horizontal(g10)
    c: Block(g10)
    c: Block(g9)
    c: Coincident(g11,g8)
    c: Horizontal(g11)
    c: Block(g12)
    c: Block(g11)
    c: Coincident(g13,g12)
    c: Coincident(g13,g9)
    c: Vertical(g13)
    c: Tangent(g13,g9)
FEATURE [Part::Extrusion] Extrude041
  Base = -> Sketch049
  Dir = (1,0,0)
  DirMode = 2
  FaceMakerClass = Part::FaceMakerBullseye
  LengthFwd = 10
  LengthRev = 0
  Placement = pos=(-2,-22.615,14.6) rot=(0,0,1;3.14159rad)
  Solid = true
  Symmetric = false
FEATURE [Part::MultiFuse] Fusion023
  Shapes = -> [Extrude039,Extrude040,Extrude041,Cut014,Fusion015]
FEATURE [Part::Extrusion] Extrude042
  Base = -> Sketch034
  Dir = (0,0.894389,-0.447291)
  DirMode = 2
  FaceMakerClass = Part::FaceMakerBullseye
  LengthFwd = 14
  LengthRev = 0
  Placement = pos=(45.5,-14,12.7) rot=(1,0,0;0.466003rad)
  Solid = true
  Symmetric = false
FEATURE [Part::Box] Box014  label="Cube014"
  AttacherType = Attacher::AttachEngine3D
  Height = 2
  Length = 2
  Placement = pos=(-12.85,-28.2,0) rot=(0,0,1;0rad)
  Width = 2
FEATURE [App::MeasureDistance] Distance005  label="Distance: 15.50 mm"
  Distance = 15.5
  P1 = (-17.5,-32.7025,2.99911)
  P2 = (-2,-32.7025,2.99911)
FEATURE [Part::Box] Box015  label="Cube015"
  AttacherType = Attacher::AttachEngine3D
  Height = 2
  Length = 2
  Placement = pos=(-10.85,-28.2,0) rot=(0,0,1;0rad)
  Width = 2
FEATURE [Part::MultiFuse] Fusion024  label="wireHoldersecondery024"
  Placement = pos=(-8.65,0,10.48) rot=(0,0,1;0rad)
  Shapes = -> [Box015,Box014]
FEATURE [App::MeasureDistance] Distance006  label="Distance: 9.44 mm"
  Distance = 9.44274
  P1 = (-8.85,-28.2,0)
  P2 = (-2,-28.1337,6.49911)
FEATURE [Part::Box] Box016  label="Cube016"
  AttacherType = Attacher::AttachEngine3D
  Height = 2
  Length = 2
  Placement = pos=(-12.85,-28.2,0) rot=(0,0,1;0rad)
  Width = 2
FEATURE [Part::Box] Box017  label="Cube017"
  AttacherType = Attacher::AttachEngine3D
  Height = 2
  Length = 2
  Placement = pos=(-10.85,-28.2,0) rot=(0,0,1;0rad)
  Width = 2
FEATURE [Part::MultiFuse] Fusion025  label="wireHoldersecondery025"
  Placement = pos=(1,0,0) rot=(0,0,1;0rad)
  Shapes = -> [Box017,Box016]
FEATURE [App::MeasureDistance] Distance007  label="Distance: 1.58 mm"
  Distance = 1.582
  P1 = (-12,-28.7025,10.4841)
  P2 = (-13.5,-28.2,10.5)
FEATURE [App::MeasureDistance] Distance008  label="Distance: 1.58 mm001"
  Distance = 1.58193
  P1 = (-13.5,-28.2,10.49)
  P2 = (-12,-28.7025,10.4841)
FEATURE [App::MeasureDistance] Distance009  label="Distance: 1.58 mm002"
  Distance = 1.58192
  P1 = (-13.5,-28.2,10.48)
  P2 = (-12,-28.7025,10.4841)
FEATURE [Part::Box] Box018  label="Cube018"
  AttacherType = Attacher::AttachEngine3D
  Height = 6.5
  Length = 8
  Placement = pos=(44,-23,2.4) rot=(0,0,1;0rad)
  Width = 6
FEATURE [Sketcher::SketchObject] Sketch050
  FullyConstrained = true
  Placement = pos=(0,-14.3,2.37) rot=(-1,0,0;2.03453rad)
  sketch-geometry (4):
    g0: LineSegment StartX=0 StartY=1.5 StartZ=0 EndX=4 EndY=1.5 EndZ=0
    g1: LineSegment StartX=4 StartY=1.5 StartZ=0 EndX=4 EndY=-2.5 EndZ=0
    g2: LineSegment StartX=4 StartY=-2.5 StartZ=0 EndX=0 EndY=-2.5 EndZ=0
    g3: LineSegment StartX=0 StartY=1.5 StartZ=0 EndX=0 EndY=-2.5 EndZ=0
  constraints (11):
    c: Horizontal(g0)
    c: Distance(g0) = 4
    c: Block(g0)
    c: Coincident(g1,g0)
    c: Vertical(g1)
    c: Distance(g1) = 4
    c: Coincident(g2,g1)
    c: Horizontal(g2)
    c: Distance(g2) = 4
    c: Coincident(g3,g0)
    c: Coincident(g3,g2)
FEATURE [Part::Cut] Cut015
  Base = -> Fusion023
  Tool = -> Box018
FEATURE [Part::Fillet] Fillet021
  Base = -> Extrude042
  Edges = 1 edges r=2: [Edge2]
FEATURE [Part::Fillet] Fillet022
  Base = -> Cut015
  Edges = 1 edges r=2: [Edge528]
FEATURE [Part::Fillet] Fillet023
  Base = -> Fillet021
  Edges = 1 edges r=1.4: [Edge12]
